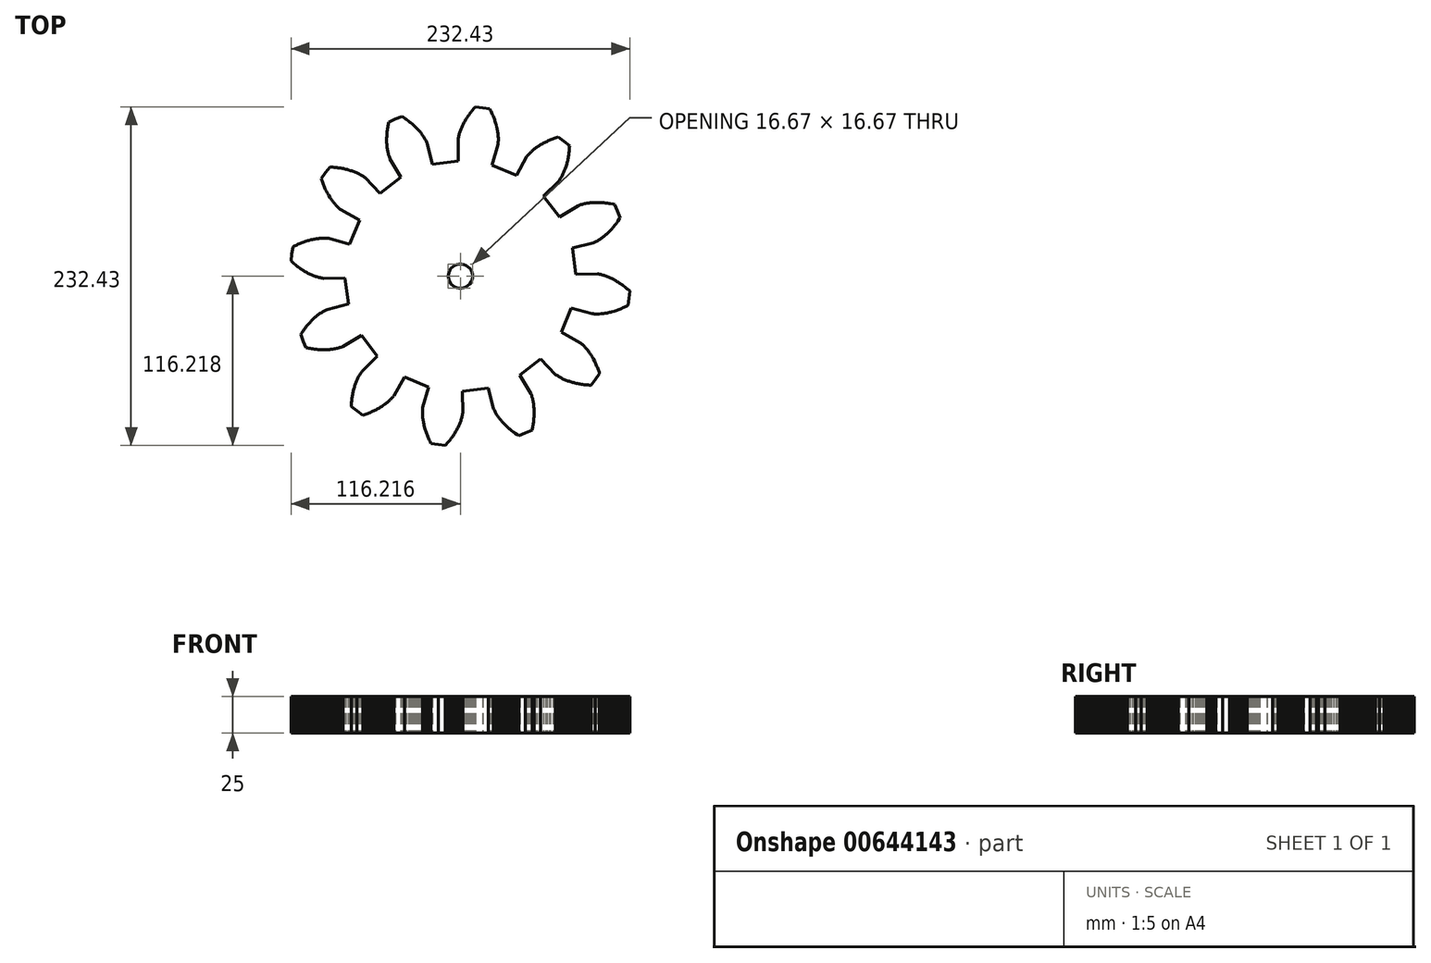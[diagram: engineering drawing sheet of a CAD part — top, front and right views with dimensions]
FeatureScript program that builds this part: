
annotation { "Feature Type Name" : "Feature", "Feature Type Description" : "" }
export const myFeature = defineFeature(function(context is Context, id is Id, definition is map)
    precondition{}
    {
        {
            var Q0;
            Q0=qCreatedBy(makeId("Top.planeOp"),FACE);
            var sketch = newSketch(context, id + "F0", { "sketchPlane" : qUnion([Q0])});
            skLineSegment(sketch, "E0", {"start": v(-581.55, 906.2) * mm, "end": v(-580.8, 906) * mm});
            skLineSegment(sketch, "E1", {"start": v(-580.8, 906) * mm, "end": v(-580.03, 905.86) * mm});
            skLineSegment(sketch, "E2", {"start": v(-580.03, 905.86) * mm, "end": v(-579.27, 905.7) * mm});
            skLineSegment(sketch, "E3", {"start": v(-579.27, 905.7) * mm, "end": v(-578.52, 905.52) * mm});
            skLineSegment(sketch, "E4", {"start": v(-578.52, 905.52) * mm, "end": v(-577.76, 905.33) * mm});
            skLineSegment(sketch, "E5", {"start": v(-577.76, 905.33) * mm, "end": v(-577, 905.1) * mm});
            skLineSegment(sketch, "E6", {"start": v(-577, 905.1) * mm, "end": v(-576.24, 904.85) * mm});
            skLineSegment(sketch, "E7", {"start": v(-576.24, 904.85) * mm, "end": v(-575.48, 904.59) * mm});
            skLineSegment(sketch, "E8", {"start": v(-575.48, 904.59) * mm, "end": v(-574.72, 904.3) * mm});
            skLineSegment(sketch, "E9", {"start": v(-574.72, 904.3) * mm, "end": v(-573.97, 904) * mm});
            skLineSegment(sketch, "E10", {"start": v(-573.97, 904) * mm, "end": v(-573.2, 903.67) * mm});
            skLineSegment(sketch, "E11", {"start": v(-573.2, 903.67) * mm, "end": v(-572.47, 903.34) * mm});
            skLineSegment(sketch, "E12", {"start": v(-572.47, 903.34) * mm, "end": v(-571.7, 902.97) * mm});
            skLineSegment(sketch, "E13", {"start": v(-571.7, 902.97) * mm, "end": v(-570.97, 902.6) * mm});
            skLineSegment(sketch, "E14", {"start": v(-570.97, 902.6) * mm, "end": v(-570.2, 902.2) * mm});
            skLineSegment(sketch, "E15", {"start": v(-570.2, 902.2) * mm, "end": v(-569.47, 901.78) * mm});
            skLineSegment(sketch, "E16", {"start": v(-569.47, 901.78) * mm, "end": v(-568.73, 901.34) * mm});
            skLineSegment(sketch, "E17", {"start": v(-568.73, 901.34) * mm, "end": v(-567.97, 900.9) * mm});
            skLineSegment(sketch, "E18", {"start": v(-567.97, 900.9) * mm, "end": v(-567.23, 900.44) * mm});
            skLineSegment(sketch, "E19", {"start": v(-567.23, 900.44) * mm, "end": v(-566.5, 899.95) * mm});
            skLineSegment(sketch, "E20", {"start": v(-566.5, 899.95) * mm, "end": v(-565.76, 899.46) * mm});
            skLineSegment(sketch, "E21", {"start": v(-565.76, 899.46) * mm, "end": v(-565.02, 898.95) * mm});
            skLineSegment(sketch, "E22", {"start": v(-565.02, 898.95) * mm, "end": v(-564.3, 898.42) * mm});
            skLineSegment(sketch, "E23", {"start": v(-564.3, 898.42) * mm, "end": v(-563.58, 897.87) * mm});
            skLineSegment(sketch, "E24", {"start": v(-563.58, 897.87) * mm, "end": v(-562.85, 897.3) * mm});
            skLineSegment(sketch, "E25", {"start": v(-562.85, 897.3) * mm, "end": v(-562.13, 896.72) * mm});
            skLineSegment(sketch, "E26", {"start": v(-562.13, 896.72) * mm, "end": v(-561.42, 896.14) * mm});
            skLineSegment(sketch, "E27", {"start": v(-561.42, 896.14) * mm, "end": v(-560.7, 895.52) * mm});
            skLineSegment(sketch, "E28", {"start": v(-560.7, 895.52) * mm, "end": v(-560, 894.9) * mm});
            skLineSegment(sketch, "E29", {"start": v(-560, 894.9) * mm, "end": v(-559.29, 894.25) * mm});
            skLineSegment(sketch, "E30", {"start": v(-559.29, 894.25) * mm, "end": v(-559.84, 889.37) * mm});
            skLineSegment(sketch, "E31", {"start": v(-559.84, 889.37) * mm, "end": v(-560.58, 884.5) * mm});
            skLineSegment(sketch, "E32", {"start": v(-560.58, 884.5) * mm, "end": v(-561.42, 884.06) * mm});
            skLineSegment(sketch, "E33", {"start": v(-561.42, 884.06) * mm, "end": v(-562.27, 883.65) * mm});
            skLineSegment(sketch, "E34", {"start": v(-562.27, 883.65) * mm, "end": v(-563.12, 883.25) * mm});
            skLineSegment(sketch, "E35", {"start": v(-563.12, 883.25) * mm, "end": v(-563.96, 882.86) * mm});
            skLineSegment(sketch, "E36", {"start": v(-563.96, 882.86) * mm, "end": v(-564.81, 882.47) * mm});
            skLineSegment(sketch, "E37", {"start": v(-564.81, 882.47) * mm, "end": v(-565.64, 882.12) * mm});
            skLineSegment(sketch, "E38", {"start": v(-565.64, 882.12) * mm, "end": v(-566.49, 881.78) * mm});
            skLineSegment(sketch, "E39", {"start": v(-566.49, 881.78) * mm, "end": v(-567.33, 881.47) * mm});
            skLineSegment(sketch, "E40", {"start": v(-567.33, 881.47) * mm, "end": v(-568.18, 881.15) * mm});
            skLineSegment(sketch, "E41", {"start": v(-568.18, 881.15) * mm, "end": v(-569, 880.87) * mm});
            skLineSegment(sketch, "E42", {"start": v(-569, 880.87) * mm, "end": v(-569.86, 880.58) * mm});
            skLineSegment(sketch, "E43", {"start": v(-569.86, 880.58) * mm, "end": v(-570.68, 880.34) * mm});
            skLineSegment(sketch, "E44", {"start": v(-570.68, 880.34) * mm, "end": v(-571.51, 880.09) * mm});
            skLineSegment(sketch, "E45", {"start": v(-571.51, 880.09) * mm, "end": v(-572.34, 879.88) * mm});
            skLineSegment(sketch, "E46", {"start": v(-572.34, 879.88) * mm, "end": v(-573.17, 879.67) * mm});
            skLineSegment(sketch, "E47", {"start": v(-573.17, 879.67) * mm, "end": v(-574, 879.47) * mm});
            skLineSegment(sketch, "E48", {"start": v(-574, 879.47) * mm, "end": v(-574.83, 879.3) * mm});
            skLineSegment(sketch, "E49", {"start": v(-574.83, 879.3) * mm, "end": v(-575.64, 879.15) * mm});
            skLineSegment(sketch, "E50", {"start": v(-575.64, 879.15) * mm, "end": v(-576.45, 879.01) * mm});
            skLineSegment(sketch, "E51", {"start": v(-576.45, 879.01) * mm, "end": v(-577.26, 878.89) * mm});
            skLineSegment(sketch, "E52", {"start": v(-577.26, 878.89) * mm, "end": v(-578.08, 878.8) * mm});
            skLineSegment(sketch, "E53", {"start": v(-578.08, 878.8) * mm, "end": v(-578.89, 878.71) * mm});
            skLineSegment(sketch, "E54", {"start": v(-578.89, 878.71) * mm, "end": v(-579.68, 878.66) * mm});
            skLineSegment(sketch, "E55", {"start": v(-579.68, 878.66) * mm, "end": v(-580.47, 878.6) * mm});
            skLineSegment(sketch, "E56", {"start": v(-580.47, 878.6) * mm, "end": v(-581.27, 878.6) * mm});
            skLineSegment(sketch, "E57", {"start": v(-581.27, 878.6) * mm, "end": v(-582.06, 878.6) * mm});
            skLineSegment(sketch, "E58", {"start": v(-582.06, 878.6) * mm, "end": v(-582.84, 878.62) * mm});
            skLineSegment(sketch, "E59", {"start": v(-582.84, 878.62) * mm, "end": v(-583.61, 878.66) * mm});
            skLineSegment(sketch, "E60", {"start": v(-583.61, 878.66) * mm, "end": v(-584.37, 878.73) * mm});
            skLineSegment(sketch, "E61", {"start": v(-584.37, 878.73) * mm, "end": v(-585.17, 878.73) * mm});
            skLineSegment(sketch, "E62", {"start": v(-585.17, 878.73) * mm, "end": v(-599.38, 882.8) * mm});
            skLineSegment(sketch, "E63", {"start": v(-599.38, 882.8) * mm, "end": v(-606.28, 866.17) * mm});
            skLineSegment(sketch, "E64", {"start": v(-606.28, 866.17) * mm, "end": v(-593.33, 859) * mm});
            skLineSegment(sketch, "E65", {"start": v(-593.33, 859) * mm, "end": v(-592.77, 858.45) * mm});
            skLineSegment(sketch, "E66", {"start": v(-592.77, 858.45) * mm, "end": v(-592.19, 857.95) * mm});
            skLineSegment(sketch, "E67", {"start": v(-592.19, 857.95) * mm, "end": v(-591.6, 857.44) * mm});
            skLineSegment(sketch, "E68", {"start": v(-591.6, 857.44) * mm, "end": v(-591.04, 856.91) * mm});
            skLineSegment(sketch, "E69", {"start": v(-591.04, 856.91) * mm, "end": v(-590.48, 856.35) * mm});
            skLineSegment(sketch, "E70", {"start": v(-590.48, 856.35) * mm, "end": v(-589.95, 855.78) * mm});
            skLineSegment(sketch, "E71", {"start": v(-589.95, 855.78) * mm, "end": v(-589.4, 855.18) * mm});
            skLineSegment(sketch, "E72", {"start": v(-589.4, 855.18) * mm, "end": v(-588.89, 854.58) * mm});
            skLineSegment(sketch, "E73", {"start": v(-588.89, 854.58) * mm, "end": v(-588.38, 853.95) * mm});
            skLineSegment(sketch, "E74", {"start": v(-588.38, 853.95) * mm, "end": v(-587.86, 853.31) * mm});
            skLineSegment(sketch, "E75", {"start": v(-587.86, 853.31) * mm, "end": v(-587.37, 852.64) * mm});
            skLineSegment(sketch, "E76", {"start": v(-587.37, 852.64) * mm, "end": v(-586.9, 851.97) * mm});
            skLineSegment(sketch, "E77", {"start": v(-586.9, 851.97) * mm, "end": v(-586.44, 851.28) * mm});
            skLineSegment(sketch, "E78", {"start": v(-586.44, 851.28) * mm, "end": v(-585.96, 850.58) * mm});
            skLineSegment(sketch, "E79", {"start": v(-585.96, 850.58) * mm, "end": v(-585.52, 849.87) * mm});
            skLineSegment(sketch, "E80", {"start": v(-585.52, 849.87) * mm, "end": v(-585.08, 849.13) * mm});
            skLineSegment(sketch, "E81", {"start": v(-585.08, 849.13) * mm, "end": v(-584.65, 848.4) * mm});
            skLineSegment(sketch, "E82", {"start": v(-584.65, 848.4) * mm, "end": v(-584.23, 847.63) * mm});
            skLineSegment(sketch, "E83", {"start": v(-584.23, 847.63) * mm, "end": v(-583.83, 846.86) * mm});
            skLineSegment(sketch, "E84", {"start": v(-583.83, 846.86) * mm, "end": v(-583.42, 846.08) * mm});
            skLineSegment(sketch, "E85", {"start": v(-583.42, 846.08) * mm, "end": v(-583.03, 845.27) * mm});
            skLineSegment(sketch, "E86", {"start": v(-583.03, 845.27) * mm, "end": v(-582.66, 844.46) * mm});
            skLineSegment(sketch, "E87", {"start": v(-582.66, 844.46) * mm, "end": v(-582.3, 843.65) * mm});
            skLineSegment(sketch, "E88", {"start": v(-582.3, 843.65) * mm, "end": v(-581.94, 842.8) * mm});
            skLineSegment(sketch, "E89", {"start": v(-581.94, 842.8) * mm, "end": v(-581.59, 841.95) * mm});
            skLineSegment(sketch, "E90", {"start": v(-581.59, 841.95) * mm, "end": v(-581.25, 841.09) * mm});
            skLineSegment(sketch, "E91", {"start": v(-581.25, 841.09) * mm, "end": v(-580.93, 840.23) * mm});
            skLineSegment(sketch, "E92", {"start": v(-580.93, 840.23) * mm, "end": v(-580.62, 839.34) * mm});
            skLineSegment(sketch, "E93", {"start": v(-580.62, 839.34) * mm, "end": v(-580.32, 838.44) * mm});
            skLineSegment(sketch, "E94", {"start": v(-580.32, 838.44) * mm, "end": v(-580.03, 837.54) * mm});
            skLineSegment(sketch, "E95", {"start": v(-580.03, 837.54) * mm, "end": v(-582.94, 833.58) * mm});
            skLineSegment(sketch, "E96", {"start": v(-582.94, 833.58) * mm, "end": v(-586.01, 829.73) * mm});
            skLineSegment(sketch, "E97", {"start": v(-586.01, 829.73) * mm, "end": v(-586.97, 829.78) * mm});
            skLineSegment(sketch, "E98", {"start": v(-586.97, 829.78) * mm, "end": v(-587.92, 829.84) * mm});
            skLineSegment(sketch, "E99", {"start": v(-587.92, 829.84) * mm, "end": v(-588.85, 829.9) * mm});
            skLineSegment(sketch, "E100", {"start": v(-588.85, 829.9) * mm, "end": v(-589.77, 830) * mm});
            skLineSegment(sketch, "E101", {"start": v(-589.77, 830) * mm, "end": v(-590.69, 830.1) * mm});
            skLineSegment(sketch, "E102", {"start": v(-590.69, 830.1) * mm, "end": v(-591.6, 830.2) * mm});
            skLineSegment(sketch, "E103", {"start": v(-591.6, 830.2) * mm, "end": v(-592.5, 830.33) * mm});
            skLineSegment(sketch, "E104", {"start": v(-592.5, 830.33) * mm, "end": v(-593.39, 830.47) * mm});
            skLineSegment(sketch, "E105", {"start": v(-593.39, 830.47) * mm, "end": v(-594.27, 830.63) * mm});
            skLineSegment(sketch, "E106", {"start": v(-594.27, 830.63) * mm, "end": v(-595.15, 830.79) * mm});
            skLineSegment(sketch, "E107", {"start": v(-595.15, 830.79) * mm, "end": v(-596.01, 830.98) * mm});
            skLineSegment(sketch, "E108", {"start": v(-596.01, 830.98) * mm, "end": v(-596.86, 831.18) * mm});
            skLineSegment(sketch, "E109", {"start": v(-596.86, 831.18) * mm, "end": v(-597.7, 831.39) * mm});
            skLineSegment(sketch, "E110", {"start": v(-597.7, 831.39) * mm, "end": v(-598.54, 831.6) * mm});
            skLineSegment(sketch, "E111", {"start": v(-598.54, 831.6) * mm, "end": v(-599.35, 831.85) * mm});
            skLineSegment(sketch, "E112", {"start": v(-599.35, 831.85) * mm, "end": v(-600.16, 832.1) * mm});
            skLineSegment(sketch, "E113", {"start": v(-600.16, 832.1) * mm, "end": v(-600.95, 832.36) * mm});
            skLineSegment(sketch, "E114", {"start": v(-600.95, 832.36) * mm, "end": v(-601.75, 832.62) * mm});
            skLineSegment(sketch, "E115", {"start": v(-601.75, 832.62) * mm, "end": v(-602.52, 832.92) * mm});
            skLineSegment(sketch, "E116", {"start": v(-602.52, 832.92) * mm, "end": v(-603.28, 833.22) * mm});
            skLineSegment(sketch, "E117", {"start": v(-603.28, 833.22) * mm, "end": v(-604.04, 833.54) * mm});
            skLineSegment(sketch, "E118", {"start": v(-604.04, 833.54) * mm, "end": v(-604.76, 833.88) * mm});
            skLineSegment(sketch, "E119", {"start": v(-604.76, 833.88) * mm, "end": v(-605.49, 834.23) * mm});
            skLineSegment(sketch, "E120", {"start": v(-605.49, 834.23) * mm, "end": v(-606.2, 834.58) * mm});
            skLineSegment(sketch, "E121", {"start": v(-606.2, 834.58) * mm, "end": v(-606.9, 834.95) * mm});
            skLineSegment(sketch, "E122", {"start": v(-606.9, 834.95) * mm, "end": v(-607.57, 835.36) * mm});
            skLineSegment(sketch, "E123", {"start": v(-607.57, 835.36) * mm, "end": v(-608.24, 835.76) * mm});
            skLineSegment(sketch, "E124", {"start": v(-608.24, 835.76) * mm, "end": v(-608.9, 836.19) * mm});
            skLineSegment(sketch, "E125", {"start": v(-608.9, 836.19) * mm, "end": v(-609.53, 836.63) * mm});
            skLineSegment(sketch, "E126", {"start": v(-609.53, 836.63) * mm, "end": v(-610.2, 837.03) * mm});
            skLineSegment(sketch, "E127", {"start": v(-610.2, 837.03) * mm, "end": v(-620.48, 847.67) * mm});
            skLineSegment(sketch, "E128", {"start": v(-620.48, 847.67) * mm, "end": v(-634.77, 836.72) * mm});
            skLineSegment(sketch, "E129", {"start": v(-634.77, 836.72) * mm, "end": v(-627.15, 824.02) * mm});
            skLineSegment(sketch, "E130", {"start": v(-627.15, 824.02) * mm, "end": v(-626.93, 823.27) * mm});
            skLineSegment(sketch, "E131", {"start": v(-626.93, 823.27) * mm, "end": v(-626.67, 822.55) * mm});
            skLineSegment(sketch, "E132", {"start": v(-626.67, 822.55) * mm, "end": v(-626.42, 821.8) * mm});
            skLineSegment(sketch, "E133", {"start": v(-626.42, 821.8) * mm, "end": v(-626.2, 821.07) * mm});
            skLineSegment(sketch, "E134", {"start": v(-626.2, 821.07) * mm, "end": v(-626, 820.31) * mm});
            skLineSegment(sketch, "E135", {"start": v(-626, 820.31) * mm, "end": v(-625.8, 819.54) * mm});
            skLineSegment(sketch, "E136", {"start": v(-625.8, 819.54) * mm, "end": v(-625.65, 818.76) * mm});
            skLineSegment(sketch, "E137", {"start": v(-625.65, 818.76) * mm, "end": v(-625.5, 817.97) * mm});
            skLineSegment(sketch, "E138", {"start": v(-625.5, 817.97) * mm, "end": v(-625.37, 817.17) * mm});
            skLineSegment(sketch, "E139", {"start": v(-625.37, 817.17) * mm, "end": v(-625.26, 816.36) * mm});
            skLineSegment(sketch, "E140", {"start": v(-625.26, 816.36) * mm, "end": v(-625.15, 815.55) * mm});
            skLineSegment(sketch, "E141", {"start": v(-625.15, 815.55) * mm, "end": v(-625.08, 814.72) * mm});
            skLineSegment(sketch, "E142", {"start": v(-625.08, 814.72) * mm, "end": v(-625.01, 813.9) * mm});
            skLineSegment(sketch, "E143", {"start": v(-625.01, 813.9) * mm, "end": v(-624.96, 813.06) * mm});
            skLineSegment(sketch, "E144", {"start": v(-624.96, 813.06) * mm, "end": v(-624.94, 812.21) * mm});
            skLineSegment(sketch, "E145", {"start": v(-624.94, 812.21) * mm, "end": v(-624.92, 811.35) * mm});
            skLineSegment(sketch, "E146", {"start": v(-624.92, 811.35) * mm, "end": v(-624.92, 810.49) * mm});
            skLineSegment(sketch, "E147", {"start": v(-624.92, 810.49) * mm, "end": v(-624.94, 809.62) * mm});
            skLineSegment(sketch, "E148", {"start": v(-624.94, 809.62) * mm, "end": v(-624.98, 808.76) * mm});
            skLineSegment(sketch, "E149", {"start": v(-624.98, 808.76) * mm, "end": v(-625.01, 807.88) * mm});
            skLineSegment(sketch, "E150", {"start": v(-625.01, 807.88) * mm, "end": v(-625.08, 807) * mm});
            skLineSegment(sketch, "E151", {"start": v(-625.08, 807) * mm, "end": v(-625.15, 806.1) * mm});
            skLineSegment(sketch, "E152", {"start": v(-625.15, 806.1) * mm, "end": v(-625.26, 805.2) * mm});
            skLineSegment(sketch, "E153", {"start": v(-625.26, 805.2) * mm, "end": v(-625.37, 804.3) * mm});
            skLineSegment(sketch, "E154", {"start": v(-625.37, 804.3) * mm, "end": v(-625.49, 803.4) * mm});
            skLineSegment(sketch, "E155", {"start": v(-625.49, 803.4) * mm, "end": v(-625.63, 802.48) * mm});
            skLineSegment(sketch, "E156", {"start": v(-625.63, 802.48) * mm, "end": v(-625.79, 801.56) * mm});
            skLineSegment(sketch, "E157", {"start": v(-625.79, 801.56) * mm, "end": v(-625.96, 800.64) * mm});
            skLineSegment(sketch, "E158", {"start": v(-625.96, 800.64) * mm, "end": v(-626.14, 799.7) * mm});
            skLineSegment(sketch, "E159", {"start": v(-626.14, 799.7) * mm, "end": v(-626.35, 798.8) * mm});
            skLineSegment(sketch, "E160", {"start": v(-626.35, 798.8) * mm, "end": v(-630.85, 796.8) * mm});
            skLineSegment(sketch, "E161", {"start": v(-630.85, 796.8) * mm, "end": v(-635.44, 795.02) * mm});
            skLineSegment(sketch, "E162", {"start": v(-635.44, 795.02) * mm, "end": v(-636.25, 795.53) * mm});
            skLineSegment(sketch, "E163", {"start": v(-636.25, 795.53) * mm, "end": v(-637.02, 796.06) * mm});
            skLineSegment(sketch, "E164", {"start": v(-637.02, 796.06) * mm, "end": v(-637.8, 796.59) * mm});
            skLineSegment(sketch, "E165", {"start": v(-637.8, 796.59) * mm, "end": v(-638.56, 797.12) * mm});
            skLineSegment(sketch, "E166", {"start": v(-638.56, 797.12) * mm, "end": v(-639.3, 797.66) * mm});
            skLineSegment(sketch, "E167", {"start": v(-639.3, 797.66) * mm, "end": v(-640.04, 798.23) * mm});
            skLineSegment(sketch, "E168", {"start": v(-640.04, 798.23) * mm, "end": v(-640.75, 798.77) * mm});
            skLineSegment(sketch, "E169", {"start": v(-640.75, 798.77) * mm, "end": v(-641.45, 799.36) * mm});
            skLineSegment(sketch, "E170", {"start": v(-641.45, 799.36) * mm, "end": v(-642.14, 799.92) * mm});
            skLineSegment(sketch, "E171", {"start": v(-642.14, 799.92) * mm, "end": v(-642.8, 800.5) * mm});
            skLineSegment(sketch, "E172", {"start": v(-642.8, 800.5) * mm, "end": v(-643.46, 801.08) * mm});
            skLineSegment(sketch, "E173", {"start": v(-643.46, 801.08) * mm, "end": v(-644.12, 801.68) * mm});
            skLineSegment(sketch, "E174", {"start": v(-644.12, 801.68) * mm, "end": v(-644.73, 802.28) * mm});
            skLineSegment(sketch, "E175", {"start": v(-644.73, 802.28) * mm, "end": v(-645.33, 802.9) * mm});
            skLineSegment(sketch, "E176", {"start": v(-645.33, 802.9) * mm, "end": v(-645.93, 803.52) * mm});
            skLineSegment(sketch, "E177", {"start": v(-645.93, 803.52) * mm, "end": v(-646.51, 804.14) * mm});
            skLineSegment(sketch, "E178", {"start": v(-646.51, 804.14) * mm, "end": v(-647.06, 804.75) * mm});
            skLineSegment(sketch, "E179", {"start": v(-647.06, 804.75) * mm, "end": v(-647.6, 805.39) * mm});
            skLineSegment(sketch, "E180", {"start": v(-647.6, 805.39) * mm, "end": v(-648.14, 806.02) * mm});
            skLineSegment(sketch, "E181", {"start": v(-648.14, 806.02) * mm, "end": v(-648.65, 806.68) * mm});
            skLineSegment(sketch, "E182", {"start": v(-648.65, 806.68) * mm, "end": v(-649.14, 807.33) * mm});
            skLineSegment(sketch, "E183", {"start": v(-649.14, 807.33) * mm, "end": v(-649.6, 807.98) * mm});
            skLineSegment(sketch, "E184", {"start": v(-649.6, 807.98) * mm, "end": v(-650.06, 808.65) * mm});
            skLineSegment(sketch, "E185", {"start": v(-650.06, 808.65) * mm, "end": v(-650.5, 809.3) * mm});
            skLineSegment(sketch, "E186", {"start": v(-650.5, 809.3) * mm, "end": v(-650.9, 810) * mm});
            skLineSegment(sketch, "E187", {"start": v(-650.9, 810) * mm, "end": v(-651.3, 810.66) * mm});
            skLineSegment(sketch, "E188", {"start": v(-651.3, 810.66) * mm, "end": v(-651.66, 811.35) * mm});
            skLineSegment(sketch, "E189", {"start": v(-651.66, 811.35) * mm, "end": v(-652.02, 812.04) * mm});
            skLineSegment(sketch, "E190", {"start": v(-652.02, 812.04) * mm, "end": v(-652.33, 812.74) * mm});
            skLineSegment(sketch, "E191", {"start": v(-652.33, 812.74) * mm, "end": v(-652.72, 813.43) * mm});
            skLineSegment(sketch, "E192", {"start": v(-652.72, 813.43) * mm, "end": v(-656.3, 827.8) * mm});
            skLineSegment(sketch, "E193", {"start": v(-656.3, 827.8) * mm, "end": v(-674.15, 825.44) * mm});
            skLineSegment(sketch, "E194", {"start": v(-674.15, 825.44) * mm, "end": v(-673.9, 810.64) * mm});
            skLineSegment(sketch, "E195", {"start": v(-673.9, 810.64) * mm, "end": v(-674.1, 809.87) * mm});
            skLineSegment(sketch, "E196", {"start": v(-674.1, 809.87) * mm, "end": v(-674.24, 809.11) * mm});
            skLineSegment(sketch, "E197", {"start": v(-674.24, 809.11) * mm, "end": v(-674.4, 808.35) * mm});
            skLineSegment(sketch, "E198", {"start": v(-674.4, 808.35) * mm, "end": v(-674.58, 807.6) * mm});
            skLineSegment(sketch, "E199", {"start": v(-674.58, 807.6) * mm, "end": v(-674.77, 806.84) * mm});
            skLineSegment(sketch, "E200", {"start": v(-674.77, 806.84) * mm, "end": v(-675, 806.08) * mm});
            skLineSegment(sketch, "E201", {"start": v(-675, 806.08) * mm, "end": v(-675.25, 805.34) * mm});
            skLineSegment(sketch, "E202", {"start": v(-675.25, 805.34) * mm, "end": v(-675.51, 804.58) * mm});
            skLineSegment(sketch, "E203", {"start": v(-675.51, 804.58) * mm, "end": v(-675.8, 803.82) * mm});
            skLineSegment(sketch, "E204", {"start": v(-675.8, 803.82) * mm, "end": v(-676.1, 803.06) * mm});
            skLineSegment(sketch, "E205", {"start": v(-676.1, 803.06) * mm, "end": v(-676.43, 802.3) * mm});
            skLineSegment(sketch, "E206", {"start": v(-676.43, 802.3) * mm, "end": v(-676.76, 801.54) * mm});
            skLineSegment(sketch, "E207", {"start": v(-676.76, 801.54) * mm, "end": v(-677.14, 800.8) * mm});
            skLineSegment(sketch, "E208", {"start": v(-677.14, 800.8) * mm, "end": v(-677.5, 800.04) * mm});
            skLineSegment(sketch, "E209", {"start": v(-677.5, 800.04) * mm, "end": v(-677.91, 799.3) * mm});
            skLineSegment(sketch, "E210", {"start": v(-677.91, 799.3) * mm, "end": v(-678.32, 798.56) * mm});
            skLineSegment(sketch, "E211", {"start": v(-678.32, 798.56) * mm, "end": v(-678.74, 797.8) * mm});
            skLineSegment(sketch, "E212", {"start": v(-678.74, 797.8) * mm, "end": v(-679.2, 797.06) * mm});
            skLineSegment(sketch, "E213", {"start": v(-679.2, 797.06) * mm, "end": v(-679.66, 796.32) * mm});
            skLineSegment(sketch, "E214", {"start": v(-679.66, 796.32) * mm, "end": v(-680.13, 795.58) * mm});
            skLineSegment(sketch, "E215", {"start": v(-680.13, 795.58) * mm, "end": v(-680.65, 794.86) * mm});
            skLineSegment(sketch, "E216", {"start": v(-680.65, 794.86) * mm, "end": v(-681.16, 794.12) * mm});
            skLineSegment(sketch, "E217", {"start": v(-681.16, 794.12) * mm, "end": v(-681.69, 793.4) * mm});
            skLineSegment(sketch, "E218", {"start": v(-681.69, 793.4) * mm, "end": v(-682.23, 792.67) * mm});
            skLineSegment(sketch, "E219", {"start": v(-682.23, 792.67) * mm, "end": v(-682.8, 791.95) * mm});
            skLineSegment(sketch, "E220", {"start": v(-682.8, 791.95) * mm, "end": v(-683.36, 791.22) * mm});
            skLineSegment(sketch, "E221", {"start": v(-683.36, 791.22) * mm, "end": v(-683.96, 790.5) * mm});
            skLineSegment(sketch, "E222", {"start": v(-683.96, 790.5) * mm, "end": v(-684.58, 789.8) * mm});
            skLineSegment(sketch, "E223", {"start": v(-684.58, 789.8) * mm, "end": v(-685.2, 789.1) * mm});
            skLineSegment(sketch, "E224", {"start": v(-685.2, 789.1) * mm, "end": v(-685.85, 788.38) * mm});
            skLineSegment(sketch, "E225", {"start": v(-685.85, 788.38) * mm, "end": v(-690.73, 788.93) * mm});
            skLineSegment(sketch, "E226", {"start": v(-690.73, 788.93) * mm, "end": v(-695.6, 789.67) * mm});
            skLineSegment(sketch, "E227", {"start": v(-695.6, 789.67) * mm, "end": v(-696.03, 790.52) * mm});
            skLineSegment(sketch, "E228", {"start": v(-696.03, 790.52) * mm, "end": v(-696.45, 791.37) * mm});
            skLineSegment(sketch, "E229", {"start": v(-696.45, 791.37) * mm, "end": v(-696.86, 792.21) * mm});
            skLineSegment(sketch, "E230", {"start": v(-696.86, 792.21) * mm, "end": v(-697.24, 793.06) * mm});
            skLineSegment(sketch, "E231", {"start": v(-697.24, 793.06) * mm, "end": v(-697.61, 793.89) * mm});
            skLineSegment(sketch, "E232", {"start": v(-697.61, 793.89) * mm, "end": v(-697.98, 794.73) * mm});
            skLineSegment(sketch, "E233", {"start": v(-697.98, 794.73) * mm, "end": v(-698.32, 795.58) * mm});
            skLineSegment(sketch, "E234", {"start": v(-698.32, 795.58) * mm, "end": v(-698.64, 796.43) * mm});
            skLineSegment(sketch, "E235", {"start": v(-698.64, 796.43) * mm, "end": v(-698.95, 797.26) * mm});
            skLineSegment(sketch, "E236", {"start": v(-698.95, 797.26) * mm, "end": v(-699.24, 798.1) * mm});
            skLineSegment(sketch, "E237", {"start": v(-699.24, 798.1) * mm, "end": v(-699.52, 798.93) * mm});
            skLineSegment(sketch, "E238", {"start": v(-699.52, 798.93) * mm, "end": v(-699.77, 799.78) * mm});
            skLineSegment(sketch, "E239", {"start": v(-699.77, 799.78) * mm, "end": v(-700.01, 800.6) * mm});
            skLineSegment(sketch, "E240", {"start": v(-700.01, 800.6) * mm, "end": v(-700.22, 801.44) * mm});
            skLineSegment(sketch, "E241", {"start": v(-700.22, 801.44) * mm, "end": v(-700.44, 802.27) * mm});
            skLineSegment(sketch, "E242", {"start": v(-700.44, 802.27) * mm, "end": v(-700.63, 803.1) * mm});
            skLineSegment(sketch, "E243", {"start": v(-700.63, 803.1) * mm, "end": v(-700.79, 803.92) * mm});
            skLineSegment(sketch, "E244", {"start": v(-700.79, 803.92) * mm, "end": v(-700.95, 804.74) * mm});
            skLineSegment(sketch, "E245", {"start": v(-700.95, 804.74) * mm, "end": v(-701.09, 805.55) * mm});
            skLineSegment(sketch, "E246", {"start": v(-701.09, 805.55) * mm, "end": v(-701.21, 806.36) * mm});
            skLineSegment(sketch, "E247", {"start": v(-701.21, 806.36) * mm, "end": v(-701.3, 807.17) * mm});
            skLineSegment(sketch, "E248", {"start": v(-701.3, 807.17) * mm, "end": v(-701.39, 807.98) * mm});
            skLineSegment(sketch, "E249", {"start": v(-701.39, 807.98) * mm, "end": v(-701.44, 808.78) * mm});
            skLineSegment(sketch, "E250", {"start": v(-701.44, 808.78) * mm, "end": v(-701.5, 809.57) * mm});
            skLineSegment(sketch, "E251", {"start": v(-701.5, 809.57) * mm, "end": v(-701.51, 810.36) * mm});
            skLineSegment(sketch, "E252", {"start": v(-701.51, 810.36) * mm, "end": v(-701.51, 811.14) * mm});
            skLineSegment(sketch, "E253", {"start": v(-701.51, 811.14) * mm, "end": v(-701.48, 811.93) * mm});
            skLineSegment(sketch, "E254", {"start": v(-701.48, 811.93) * mm, "end": v(-701.44, 812.7) * mm});
            skLineSegment(sketch, "E255", {"start": v(-701.44, 812.7) * mm, "end": v(-701.37, 813.47) * mm});
            skLineSegment(sketch, "E256", {"start": v(-701.37, 813.47) * mm, "end": v(-701.35, 814.24) * mm});
            skLineSegment(sketch, "E257", {"start": v(-701.35, 814.24) * mm, "end": v(-697.28, 828.48) * mm});
            skLineSegment(sketch, "E258", {"start": v(-697.28, 828.48) * mm, "end": v(-713.93, 835.37) * mm});
            skLineSegment(sketch, "E259", {"start": v(-713.93, 835.37) * mm, "end": v(-721.1, 822.43) * mm});
            skLineSegment(sketch, "E260", {"start": v(-721.1, 822.43) * mm, "end": v(-721.66, 821.86) * mm});
            skLineSegment(sketch, "E261", {"start": v(-721.66, 821.86) * mm, "end": v(-722.15, 821.28) * mm});
            skLineSegment(sketch, "E262", {"start": v(-722.15, 821.28) * mm, "end": v(-722.66, 820.7) * mm});
            skLineSegment(sketch, "E263", {"start": v(-722.66, 820.7) * mm, "end": v(-723.2, 820.13) * mm});
            skLineSegment(sketch, "E264", {"start": v(-723.2, 820.13) * mm, "end": v(-723.75, 819.57) * mm});
            skLineSegment(sketch, "E265", {"start": v(-723.75, 819.57) * mm, "end": v(-724.32, 819.02) * mm});
            skLineSegment(sketch, "E266", {"start": v(-724.32, 819.02) * mm, "end": v(-724.92, 818.5) * mm});
            skLineSegment(sketch, "E267", {"start": v(-724.92, 818.5) * mm, "end": v(-725.52, 817.98) * mm});
            skLineSegment(sketch, "E268", {"start": v(-725.52, 817.98) * mm, "end": v(-726.15, 817.47) * mm});
            skLineSegment(sketch, "E269", {"start": v(-726.15, 817.47) * mm, "end": v(-726.79, 816.96) * mm});
            skLineSegment(sketch, "E270", {"start": v(-726.79, 816.96) * mm, "end": v(-727.44, 816.47) * mm});
            skLineSegment(sketch, "E271", {"start": v(-727.44, 816.47) * mm, "end": v(-728.13, 815.99) * mm});
            skLineSegment(sketch, "E272", {"start": v(-728.13, 815.99) * mm, "end": v(-728.82, 815.51) * mm});
            skLineSegment(sketch, "E273", {"start": v(-728.82, 815.51) * mm, "end": v(-729.5, 815.05) * mm});
            skLineSegment(sketch, "E274", {"start": v(-729.5, 815.05) * mm, "end": v(-730.23, 814.61) * mm});
            skLineSegment(sketch, "E275", {"start": v(-730.23, 814.61) * mm, "end": v(-730.97, 814.17) * mm});
            skLineSegment(sketch, "E276", {"start": v(-730.97, 814.17) * mm, "end": v(-731.7, 813.73) * mm});
            skLineSegment(sketch, "E277", {"start": v(-731.7, 813.73) * mm, "end": v(-732.47, 813.33) * mm});
            skLineSegment(sketch, "E278", {"start": v(-732.47, 813.33) * mm, "end": v(-733.24, 812.9) * mm});
            skLineSegment(sketch, "E279", {"start": v(-733.24, 812.9) * mm, "end": v(-734.02, 812.51) * mm});
            skLineSegment(sketch, "E280", {"start": v(-734.02, 812.51) * mm, "end": v(-734.81, 812.13) * mm});
            skLineSegment(sketch, "E281", {"start": v(-734.81, 812.13) * mm, "end": v(-735.63, 811.76) * mm});
            skLineSegment(sketch, "E282", {"start": v(-735.63, 811.76) * mm, "end": v(-736.45, 811.38) * mm});
            skLineSegment(sketch, "E283", {"start": v(-736.45, 811.38) * mm, "end": v(-737.3, 811.03) * mm});
            skLineSegment(sketch, "E284", {"start": v(-737.3, 811.03) * mm, "end": v(-738.15, 810.68) * mm});
            skLineSegment(sketch, "E285", {"start": v(-738.15, 810.68) * mm, "end": v(-739, 810.35) * mm});
            skLineSegment(sketch, "E286", {"start": v(-739, 810.35) * mm, "end": v(-739.88, 810.03) * mm});
            skLineSegment(sketch, "E287", {"start": v(-739.88, 810.03) * mm, "end": v(-740.76, 809.7) * mm});
            skLineSegment(sketch, "E288", {"start": v(-740.76, 809.7) * mm, "end": v(-741.66, 809.41) * mm});
            skLineSegment(sketch, "E289", {"start": v(-741.66, 809.41) * mm, "end": v(-742.56, 809.13) * mm});
            skLineSegment(sketch, "E290", {"start": v(-742.56, 809.13) * mm, "end": v(-746.53, 812.04) * mm});
            skLineSegment(sketch, "E291", {"start": v(-746.53, 812.04) * mm, "end": v(-750.37, 815.1) * mm});
            skLineSegment(sketch, "E292", {"start": v(-750.37, 815.1) * mm, "end": v(-750.32, 816.06) * mm});
            skLineSegment(sketch, "E293", {"start": v(-750.32, 816.06) * mm, "end": v(-750.27, 817.01) * mm});
            skLineSegment(sketch, "E294", {"start": v(-750.27, 817.01) * mm, "end": v(-750.2, 817.95) * mm});
            skLineSegment(sketch, "E295", {"start": v(-750.2, 817.95) * mm, "end": v(-750.1, 818.86) * mm});
            skLineSegment(sketch, "E296", {"start": v(-750.1, 818.86) * mm, "end": v(-750, 819.78) * mm});
            skLineSegment(sketch, "E297", {"start": v(-750, 819.78) * mm, "end": v(-749.9, 820.7) * mm});
            skLineSegment(sketch, "E298", {"start": v(-749.9, 820.7) * mm, "end": v(-749.77, 821.6) * mm});
            skLineSegment(sketch, "E299", {"start": v(-749.77, 821.6) * mm, "end": v(-749.63, 822.48) * mm});
            skLineSegment(sketch, "E300", {"start": v(-749.63, 822.48) * mm, "end": v(-749.47, 823.36) * mm});
            skLineSegment(sketch, "E301", {"start": v(-749.47, 823.36) * mm, "end": v(-749.3, 824.24) * mm});
            skLineSegment(sketch, "E302", {"start": v(-749.3, 824.24) * mm, "end": v(-749.12, 825.1) * mm});
            skLineSegment(sketch, "E303", {"start": v(-749.12, 825.1) * mm, "end": v(-748.93, 825.96) * mm});
            skLineSegment(sketch, "E304", {"start": v(-748.93, 825.96) * mm, "end": v(-748.71, 826.78) * mm});
            skLineSegment(sketch, "E305", {"start": v(-748.71, 826.78) * mm, "end": v(-748.5, 827.63) * mm});
            skLineSegment(sketch, "E306", {"start": v(-748.5, 827.63) * mm, "end": v(-748.26, 828.44) * mm});
            skLineSegment(sketch, "E307", {"start": v(-748.26, 828.44) * mm, "end": v(-748, 829.25) * mm});
            skLineSegment(sketch, "E308", {"start": v(-748, 829.25) * mm, "end": v(-747.74, 830.05) * mm});
            skLineSegment(sketch, "E309", {"start": v(-747.74, 830.05) * mm, "end": v(-747.48, 830.84) * mm});
            skLineSegment(sketch, "E310", {"start": v(-747.48, 830.84) * mm, "end": v(-747.18, 831.62) * mm});
            skLineSegment(sketch, "E311", {"start": v(-747.18, 831.62) * mm, "end": v(-746.88, 832.38) * mm});
            skLineSegment(sketch, "E312", {"start": v(-746.88, 832.38) * mm, "end": v(-746.56, 833.12) * mm});
            skLineSegment(sketch, "E313", {"start": v(-746.56, 833.12) * mm, "end": v(-746.23, 833.86) * mm});
            skLineSegment(sketch, "E314", {"start": v(-746.23, 833.86) * mm, "end": v(-745.87, 834.58) * mm});
            skLineSegment(sketch, "E315", {"start": v(-745.87, 834.58) * mm, "end": v(-745.52, 835.29) * mm});
            skLineSegment(sketch, "E316", {"start": v(-745.52, 835.29) * mm, "end": v(-745.13, 836) * mm});
            skLineSegment(sketch, "E317", {"start": v(-745.13, 836) * mm, "end": v(-744.75, 836.66) * mm});
            skLineSegment(sketch, "E318", {"start": v(-744.75, 836.66) * mm, "end": v(-744.34, 837.33) * mm});
            skLineSegment(sketch, "E319", {"start": v(-744.34, 837.33) * mm, "end": v(-743.92, 837.99) * mm});
            skLineSegment(sketch, "E320", {"start": v(-743.92, 837.99) * mm, "end": v(-743.48, 838.6) * mm});
            skLineSegment(sketch, "E321", {"start": v(-743.48, 838.6) * mm, "end": v(-743.07, 839.3) * mm});
            skLineSegment(sketch, "E322", {"start": v(-743.07, 839.3) * mm, "end": v(-732.43, 849.57) * mm});
            skLineSegment(sketch, "E323", {"start": v(-732.43, 849.57) * mm, "end": v(-743.39, 863.86) * mm});
            skLineSegment(sketch, "E324", {"start": v(-743.39, 863.86) * mm, "end": v(-756.09, 856.24) * mm});
            skLineSegment(sketch, "E325", {"start": v(-756.09, 856.24) * mm, "end": v(-756.83, 856.03) * mm});
            skLineSegment(sketch, "E326", {"start": v(-756.83, 856.03) * mm, "end": v(-757.55, 855.76) * mm});
            skLineSegment(sketch, "E327", {"start": v(-757.55, 855.76) * mm, "end": v(-758.3, 855.52) * mm});
            skLineSegment(sketch, "E328", {"start": v(-758.3, 855.52) * mm, "end": v(-759.03, 855.29) * mm});
            skLineSegment(sketch, "E329", {"start": v(-759.03, 855.29) * mm, "end": v(-759.8, 855.1) * mm});
            skLineSegment(sketch, "E330", {"start": v(-759.8, 855.1) * mm, "end": v(-760.57, 854.9) * mm});
            skLineSegment(sketch, "E331", {"start": v(-760.57, 854.9) * mm, "end": v(-761.34, 854.74) * mm});
            skLineSegment(sketch, "E332", {"start": v(-761.34, 854.74) * mm, "end": v(-762.14, 854.58) * mm});
            skLineSegment(sketch, "E333", {"start": v(-762.14, 854.58) * mm, "end": v(-762.93, 854.46) * mm});
            skLineSegment(sketch, "E334", {"start": v(-762.93, 854.46) * mm, "end": v(-763.74, 854.35) * mm});
            skLineSegment(sketch, "E335", {"start": v(-763.74, 854.35) * mm, "end": v(-764.55, 854.25) * mm});
            skLineSegment(sketch, "E336", {"start": v(-764.55, 854.25) * mm, "end": v(-765.38, 854.18) * mm});
            skLineSegment(sketch, "E337", {"start": v(-765.38, 854.18) * mm, "end": v(-766.21, 854.1) * mm});
            skLineSegment(sketch, "E338", {"start": v(-766.21, 854.1) * mm, "end": v(-767.04, 854.05) * mm});
            skLineSegment(sketch, "E339", {"start": v(-767.04, 854.05) * mm, "end": v(-767.89, 854.04) * mm});
            skLineSegment(sketch, "E340", {"start": v(-767.89, 854.04) * mm, "end": v(-768.75, 854.02) * mm});
            skLineSegment(sketch, "E341", {"start": v(-768.75, 854.02) * mm, "end": v(-769.6, 854.02) * mm});
            skLineSegment(sketch, "E342", {"start": v(-769.6, 854.02) * mm, "end": v(-770.48, 854.04) * mm});
            skLineSegment(sketch, "E343", {"start": v(-770.48, 854.04) * mm, "end": v(-771.34, 854.05) * mm});
            skLineSegment(sketch, "E344", {"start": v(-771.34, 854.05) * mm, "end": v(-772.23, 854.1) * mm});
            skLineSegment(sketch, "E345", {"start": v(-772.23, 854.1) * mm, "end": v(-773.1, 854.18) * mm});
            skLineSegment(sketch, "E346", {"start": v(-773.1, 854.18) * mm, "end": v(-774, 854.25) * mm});
            skLineSegment(sketch, "E347", {"start": v(-774, 854.25) * mm, "end": v(-774.89, 854.35) * mm});
            skLineSegment(sketch, "E348", {"start": v(-774.89, 854.35) * mm, "end": v(-775.8, 854.46) * mm});
            skLineSegment(sketch, "E349", {"start": v(-775.8, 854.46) * mm, "end": v(-776.7, 854.58) * mm});
            skLineSegment(sketch, "E350", {"start": v(-776.7, 854.58) * mm, "end": v(-777.62, 854.72) * mm});
            skLineSegment(sketch, "E351", {"start": v(-777.62, 854.72) * mm, "end": v(-778.54, 854.88) * mm});
            skLineSegment(sketch, "E352", {"start": v(-778.54, 854.88) * mm, "end": v(-779.46, 855.06) * mm});
            skLineSegment(sketch, "E353", {"start": v(-779.46, 855.06) * mm, "end": v(-780.4, 855.24) * mm});
            skLineSegment(sketch, "E354", {"start": v(-780.4, 855.24) * mm, "end": v(-781.31, 855.45) * mm});
            skLineSegment(sketch, "E355", {"start": v(-781.31, 855.45) * mm, "end": v(-783.29, 859.95) * mm});
            skLineSegment(sketch, "E356", {"start": v(-783.29, 859.95) * mm, "end": v(-785.09, 864.53) * mm});
            skLineSegment(sketch, "E357", {"start": v(-785.09, 864.53) * mm, "end": v(-784.57, 865.33) * mm});
            skLineSegment(sketch, "E358", {"start": v(-784.57, 865.33) * mm, "end": v(-784.04, 866.12) * mm});
            skLineSegment(sketch, "E359", {"start": v(-784.04, 866.12) * mm, "end": v(-783.52, 866.9) * mm});
            skLineSegment(sketch, "E360", {"start": v(-783.52, 866.9) * mm, "end": v(-782.97, 867.65) * mm});
            skLineSegment(sketch, "E361", {"start": v(-782.97, 867.65) * mm, "end": v(-782.44, 868.4) * mm});
            skLineSegment(sketch, "E362", {"start": v(-782.44, 868.4) * mm, "end": v(-781.87, 869.14) * mm});
            skLineSegment(sketch, "E363", {"start": v(-781.87, 869.14) * mm, "end": v(-781.31, 869.84) * mm});
            skLineSegment(sketch, "E364", {"start": v(-781.31, 869.84) * mm, "end": v(-780.75, 870.55) * mm});
            skLineSegment(sketch, "E365", {"start": v(-780.75, 870.55) * mm, "end": v(-780.18, 871.23) * mm});
            skLineSegment(sketch, "E366", {"start": v(-780.18, 871.23) * mm, "end": v(-779.6, 871.9) * mm});
            skLineSegment(sketch, "E367", {"start": v(-779.6, 871.9) * mm, "end": v(-779, 872.56) * mm});
            skLineSegment(sketch, "E368", {"start": v(-779, 872.56) * mm, "end": v(-778.42, 873.2) * mm});
            skLineSegment(sketch, "E369", {"start": v(-778.42, 873.2) * mm, "end": v(-777.82, 873.83) * mm});
            skLineSegment(sketch, "E370", {"start": v(-777.82, 873.83) * mm, "end": v(-777.2, 874.43) * mm});
            skLineSegment(sketch, "E371", {"start": v(-777.2, 874.43) * mm, "end": v(-776.58, 875.03) * mm});
            skLineSegment(sketch, "E372", {"start": v(-776.58, 875.03) * mm, "end": v(-775.97, 875.6) * mm});
            skLineSegment(sketch, "E373", {"start": v(-775.97, 875.6) * mm, "end": v(-775.35, 876.16) * mm});
            skLineSegment(sketch, "E374", {"start": v(-775.35, 876.16) * mm, "end": v(-774.71, 876.7) * mm});
            skLineSegment(sketch, "E375", {"start": v(-774.71, 876.7) * mm, "end": v(-774.08, 877.23) * mm});
            skLineSegment(sketch, "E376", {"start": v(-774.08, 877.23) * mm, "end": v(-773.43, 877.74) * mm});
            skLineSegment(sketch, "E377", {"start": v(-773.43, 877.74) * mm, "end": v(-772.77, 878.22) * mm});
            skLineSegment(sketch, "E378", {"start": v(-772.77, 878.22) * mm, "end": v(-772.12, 878.7) * mm});
            skLineSegment(sketch, "E379", {"start": v(-772.12, 878.7) * mm, "end": v(-771.45, 879.15) * mm});
            skLineSegment(sketch, "E380", {"start": v(-771.45, 879.15) * mm, "end": v(-770.78, 879.58) * mm});
            skLineSegment(sketch, "E381", {"start": v(-770.78, 879.58) * mm, "end": v(-770.1, 880) * mm});
            skLineSegment(sketch, "E382", {"start": v(-770.1, 880) * mm, "end": v(-769.44, 880.39) * mm});
            skLineSegment(sketch, "E383", {"start": v(-769.44, 880.39) * mm, "end": v(-768.75, 880.76) * mm});
            skLineSegment(sketch, "E384", {"start": v(-768.75, 880.76) * mm, "end": v(-768.06, 881.11) * mm});
            skLineSegment(sketch, "E385", {"start": v(-768.06, 881.11) * mm, "end": v(-767.36, 881.43) * mm});
            skLineSegment(sketch, "E386", {"start": v(-767.36, 881.43) * mm, "end": v(-766.67, 881.82) * mm});
            skLineSegment(sketch, "E387", {"start": v(-766.67, 881.82) * mm, "end": v(-752.31, 885.4) * mm});
            skLineSegment(sketch, "E388", {"start": v(-752.31, 885.4) * mm, "end": v(-754.66, 903.25) * mm});
            skLineSegment(sketch, "E389", {"start": v(-754.66, 903.25) * mm, "end": v(-769.46, 903) * mm});
            skLineSegment(sketch, "E390", {"start": v(-769.46, 903) * mm, "end": v(-770.22, 903.2) * mm});
            skLineSegment(sketch, "E391", {"start": v(-770.22, 903.2) * mm, "end": v(-770.97, 903.34) * mm});
            skLineSegment(sketch, "E392", {"start": v(-770.97, 903.34) * mm, "end": v(-771.73, 903.48) * mm});
            skLineSegment(sketch, "E393", {"start": v(-771.73, 903.48) * mm, "end": v(-772.5, 903.67) * mm});
            skLineSegment(sketch, "E394", {"start": v(-772.5, 903.67) * mm, "end": v(-773.25, 903.87) * mm});
            skLineSegment(sketch, "E395", {"start": v(-773.25, 903.87) * mm, "end": v(-774, 904.1) * mm});
            skLineSegment(sketch, "E396", {"start": v(-774, 904.1) * mm, "end": v(-774.77, 904.34) * mm});
            skLineSegment(sketch, "E397", {"start": v(-774.77, 904.34) * mm, "end": v(-775.52, 904.6) * mm});
            skLineSegment(sketch, "E398", {"start": v(-775.52, 904.6) * mm, "end": v(-776.28, 904.89) * mm});
            skLineSegment(sketch, "E399", {"start": v(-776.28, 904.89) * mm, "end": v(-777.04, 905.19) * mm});
            skLineSegment(sketch, "E400", {"start": v(-777.04, 905.19) * mm, "end": v(-777.8, 905.52) * mm});
            skLineSegment(sketch, "E401", {"start": v(-777.8, 905.52) * mm, "end": v(-778.54, 905.86) * mm});
            skLineSegment(sketch, "E402", {"start": v(-778.54, 905.86) * mm, "end": v(-779.3, 906.23) * mm});
            skLineSegment(sketch, "E403", {"start": v(-779.3, 906.23) * mm, "end": v(-780.06, 906.6) * mm});
            skLineSegment(sketch, "E404", {"start": v(-780.06, 906.6) * mm, "end": v(-780.8, 906.99) * mm});
            skLineSegment(sketch, "E405", {"start": v(-780.8, 906.99) * mm, "end": v(-781.54, 907.41) * mm});
            skLineSegment(sketch, "E406", {"start": v(-781.54, 907.41) * mm, "end": v(-782.3, 907.84) * mm});
            skLineSegment(sketch, "E407", {"start": v(-782.3, 907.84) * mm, "end": v(-783.04, 908.3) * mm});
            skLineSegment(sketch, "E408", {"start": v(-783.04, 908.3) * mm, "end": v(-783.78, 908.75) * mm});
            skLineSegment(sketch, "E409", {"start": v(-783.78, 908.75) * mm, "end": v(-784.5, 909.23) * mm});
            skLineSegment(sketch, "E410", {"start": v(-784.5, 909.23) * mm, "end": v(-785.24, 909.72) * mm});
            skLineSegment(sketch, "E411", {"start": v(-785.24, 909.72) * mm, "end": v(-785.98, 910.25) * mm});
            skLineSegment(sketch, "E412", {"start": v(-785.98, 910.25) * mm, "end": v(-786.7, 910.78) * mm});
            skLineSegment(sketch, "E413", {"start": v(-786.7, 910.78) * mm, "end": v(-787.43, 911.33) * mm});
            skLineSegment(sketch, "E414", {"start": v(-787.43, 911.33) * mm, "end": v(-788.15, 911.9) * mm});
            skLineSegment(sketch, "E415", {"start": v(-788.15, 911.9) * mm, "end": v(-788.88, 912.46) * mm});
            skLineSegment(sketch, "E416", {"start": v(-788.88, 912.46) * mm, "end": v(-789.58, 913.06) * mm});
            skLineSegment(sketch, "E417", {"start": v(-789.58, 913.06) * mm, "end": v(-790.3, 913.67) * mm});
            skLineSegment(sketch, "E418", {"start": v(-790.3, 913.67) * mm, "end": v(-791.01, 914.3) * mm});
            skLineSegment(sketch, "E419", {"start": v(-791.01, 914.3) * mm, "end": v(-791.72, 914.93) * mm});
            skLineSegment(sketch, "E420", {"start": v(-791.72, 914.93) * mm, "end": v(-791.17, 919.83) * mm});
            skLineSegment(sketch, "E421", {"start": v(-791.17, 919.83) * mm, "end": v(-790.43, 924.68) * mm});
            skLineSegment(sketch, "E422", {"start": v(-790.43, 924.68) * mm, "end": v(-789.58, 925.12) * mm});
            skLineSegment(sketch, "E423", {"start": v(-789.58, 925.12) * mm, "end": v(-788.74, 925.54) * mm});
            skLineSegment(sketch, "E424", {"start": v(-788.74, 925.54) * mm, "end": v(-787.89, 925.95) * mm});
            skLineSegment(sketch, "E425", {"start": v(-787.89, 925.95) * mm, "end": v(-787.04, 926.34) * mm});
            skLineSegment(sketch, "E426", {"start": v(-787.04, 926.34) * mm, "end": v(-786.2, 926.7) * mm});
            skLineSegment(sketch, "E427", {"start": v(-786.2, 926.7) * mm, "end": v(-785.37, 927.06) * mm});
            skLineSegment(sketch, "E428", {"start": v(-785.37, 927.06) * mm, "end": v(-784.52, 927.41) * mm});
            skLineSegment(sketch, "E429", {"start": v(-784.52, 927.41) * mm, "end": v(-783.67, 927.73) * mm});
            skLineSegment(sketch, "E430", {"start": v(-783.67, 927.73) * mm, "end": v(-782.83, 928.03) * mm});
            skLineSegment(sketch, "E431", {"start": v(-782.83, 928.03) * mm, "end": v(-782, 928.33) * mm});
            skLineSegment(sketch, "E432", {"start": v(-782, 928.33) * mm, "end": v(-781.15, 928.6) * mm});
            skLineSegment(sketch, "E433", {"start": v(-781.15, 928.6) * mm, "end": v(-780.32, 928.86) * mm});
            skLineSegment(sketch, "E434", {"start": v(-780.32, 928.86) * mm, "end": v(-779.5, 929.1) * mm});
            skLineSegment(sketch, "E435", {"start": v(-779.5, 929.1) * mm, "end": v(-778.66, 929.32) * mm});
            skLineSegment(sketch, "E436", {"start": v(-778.66, 929.32) * mm, "end": v(-777.84, 929.53) * mm});
            skLineSegment(sketch, "E437", {"start": v(-777.84, 929.53) * mm, "end": v(-777, 929.72) * mm});
            skLineSegment(sketch, "E438", {"start": v(-777, 929.72) * mm, "end": v(-776.18, 929.88) * mm});
            skLineSegment(sketch, "E439", {"start": v(-776.18, 929.88) * mm, "end": v(-775.37, 930.04) * mm});
            skLineSegment(sketch, "E440", {"start": v(-775.37, 930.04) * mm, "end": v(-774.55, 930.18) * mm});
            skLineSegment(sketch, "E441", {"start": v(-774.55, 930.18) * mm, "end": v(-773.74, 930.29) * mm});
            skLineSegment(sketch, "E442", {"start": v(-773.74, 930.29) * mm, "end": v(-772.93, 930.4) * mm});
            skLineSegment(sketch, "E443", {"start": v(-772.93, 930.4) * mm, "end": v(-772.12, 930.48) * mm});
            skLineSegment(sketch, "E444", {"start": v(-772.12, 930.48) * mm, "end": v(-771.33, 930.54) * mm});
            skLineSegment(sketch, "E445", {"start": v(-771.33, 930.54) * mm, "end": v(-770.53, 930.57) * mm});
            skLineSegment(sketch, "E446", {"start": v(-770.53, 930.57) * mm, "end": v(-769.74, 930.6) * mm});
            skLineSegment(sketch, "E447", {"start": v(-769.74, 930.6) * mm, "end": v(-768.95, 930.6) * mm});
            skLineSegment(sketch, "E448", {"start": v(-768.95, 930.6) * mm, "end": v(-768.17, 930.57) * mm});
            skLineSegment(sketch, "E449", {"start": v(-768.17, 930.57) * mm, "end": v(-767.4, 930.54) * mm});
            skLineSegment(sketch, "E450", {"start": v(-767.4, 930.54) * mm, "end": v(-766.63, 930.47) * mm});
            skLineSegment(sketch, "E451", {"start": v(-766.63, 930.47) * mm, "end": v(-765.84, 930.45) * mm});
            skLineSegment(sketch, "E452", {"start": v(-765.84, 930.45) * mm, "end": v(-751.62, 926.37) * mm});
            skLineSegment(sketch, "E453", {"start": v(-751.62, 926.37) * mm, "end": v(-744.73, 943) * mm});
            skLineSegment(sketch, "E454", {"start": v(-744.73, 943) * mm, "end": v(-757.67, 950.2) * mm});
            skLineSegment(sketch, "E455", {"start": v(-757.67, 950.2) * mm, "end": v(-758.24, 950.75) * mm});
            skLineSegment(sketch, "E456", {"start": v(-758.24, 950.75) * mm, "end": v(-758.82, 951.24) * mm});
            skLineSegment(sketch, "E457", {"start": v(-758.82, 951.24) * mm, "end": v(-759.4, 951.76) * mm});
            skLineSegment(sketch, "E458", {"start": v(-759.4, 951.76) * mm, "end": v(-759.97, 952.28) * mm});
            skLineSegment(sketch, "E459", {"start": v(-759.97, 952.28) * mm, "end": v(-760.53, 952.85) * mm});
            skLineSegment(sketch, "E460", {"start": v(-760.53, 952.85) * mm, "end": v(-761.06, 953.41) * mm});
            skLineSegment(sketch, "E461", {"start": v(-761.06, 953.41) * mm, "end": v(-761.6, 954.01) * mm});
            skLineSegment(sketch, "E462", {"start": v(-761.6, 954.01) * mm, "end": v(-762.12, 954.61) * mm});
            skLineSegment(sketch, "E463", {"start": v(-762.12, 954.61) * mm, "end": v(-762.63, 955.25) * mm});
            skLineSegment(sketch, "E464", {"start": v(-762.63, 955.25) * mm, "end": v(-763.14, 955.88) * mm});
            skLineSegment(sketch, "E465", {"start": v(-763.14, 955.88) * mm, "end": v(-763.64, 956.54) * mm});
            skLineSegment(sketch, "E466", {"start": v(-763.64, 956.54) * mm, "end": v(-764.11, 957.2) * mm});
            skLineSegment(sketch, "E467", {"start": v(-764.11, 957.2) * mm, "end": v(-764.59, 957.9) * mm});
            skLineSegment(sketch, "E468", {"start": v(-764.59, 957.9) * mm, "end": v(-765.05, 958.6) * mm});
            skLineSegment(sketch, "E469", {"start": v(-765.05, 958.6) * mm, "end": v(-765.49, 959.32) * mm});
            skLineSegment(sketch, "E470", {"start": v(-765.49, 959.32) * mm, "end": v(-765.93, 960.05) * mm});
            skLineSegment(sketch, "E471", {"start": v(-765.93, 960.05) * mm, "end": v(-766.35, 960.8) * mm});
            skLineSegment(sketch, "E472", {"start": v(-766.35, 960.8) * mm, "end": v(-766.78, 961.56) * mm});
            skLineSegment(sketch, "E473", {"start": v(-766.78, 961.56) * mm, "end": v(-767.18, 962.32) * mm});
            skLineSegment(sketch, "E474", {"start": v(-767.18, 962.32) * mm, "end": v(-767.59, 963.12) * mm});
            skLineSegment(sketch, "E475", {"start": v(-767.59, 963.12) * mm, "end": v(-767.98, 963.9) * mm});
            skLineSegment(sketch, "E476", {"start": v(-767.98, 963.9) * mm, "end": v(-768.35, 964.72) * mm});
            skLineSegment(sketch, "E477", {"start": v(-768.35, 964.72) * mm, "end": v(-768.72, 965.55) * mm});
            skLineSegment(sketch, "E478", {"start": v(-768.72, 965.55) * mm, "end": v(-769.07, 966.38) * mm});
            skLineSegment(sketch, "E479", {"start": v(-769.07, 966.38) * mm, "end": v(-769.42, 967.22) * mm});
            skLineSegment(sketch, "E480", {"start": v(-769.42, 967.22) * mm, "end": v(-769.76, 968.09) * mm});
            skLineSegment(sketch, "E481", {"start": v(-769.76, 968.09) * mm, "end": v(-770.07, 968.97) * mm});
            skLineSegment(sketch, "E482", {"start": v(-770.07, 968.97) * mm, "end": v(-770.4, 969.85) * mm});
            skLineSegment(sketch, "E483", {"start": v(-770.4, 969.85) * mm, "end": v(-770.7, 970.75) * mm});
            skLineSegment(sketch, "E484", {"start": v(-770.7, 970.75) * mm, "end": v(-770.97, 971.65) * mm});
            skLineSegment(sketch, "E485", {"start": v(-770.97, 971.65) * mm, "end": v(-768.06, 975.62) * mm});
            skLineSegment(sketch, "E486", {"start": v(-768.06, 975.62) * mm, "end": v(-765, 979.47) * mm});
            skLineSegment(sketch, "E487", {"start": v(-765, 979.47) * mm, "end": v(-764.04, 979.41) * mm});
            skLineSegment(sketch, "E488", {"start": v(-764.04, 979.41) * mm, "end": v(-763.09, 979.36) * mm});
            skLineSegment(sketch, "E489", {"start": v(-763.09, 979.36) * mm, "end": v(-762.15, 979.3) * mm});
            skLineSegment(sketch, "E490", {"start": v(-762.15, 979.3) * mm, "end": v(-761.24, 979.2) * mm});
            skLineSegment(sketch, "E491", {"start": v(-761.24, 979.2) * mm, "end": v(-760.32, 979.1) * mm});
            skLineSegment(sketch, "E492", {"start": v(-760.32, 979.1) * mm, "end": v(-759.4, 979) * mm});
            skLineSegment(sketch, "E493", {"start": v(-759.4, 979) * mm, "end": v(-758.5, 978.87) * mm});
            skLineSegment(sketch, "E494", {"start": v(-758.5, 978.87) * mm, "end": v(-757.62, 978.73) * mm});
            skLineSegment(sketch, "E495", {"start": v(-757.62, 978.73) * mm, "end": v(-756.74, 978.57) * mm});
            skLineSegment(sketch, "E496", {"start": v(-756.74, 978.57) * mm, "end": v(-755.86, 978.39) * mm});
            skLineSegment(sketch, "E497", {"start": v(-755.86, 978.39) * mm, "end": v(-755, 978.21) * mm});
            skLineSegment(sketch, "E498", {"start": v(-755, 978.21) * mm, "end": v(-754.15, 978.02) * mm});
            skLineSegment(sketch, "E499", {"start": v(-754.15, 978.02) * mm, "end": v(-753.3, 977.8) * mm});
            skLineSegment(sketch, "E500", {"start": v(-753.3, 977.8) * mm, "end": v(-752.47, 977.6) * mm});
            skLineSegment(sketch, "E501", {"start": v(-752.47, 977.6) * mm, "end": v(-751.66, 977.35) * mm});
            skLineSegment(sketch, "E502", {"start": v(-751.66, 977.35) * mm, "end": v(-750.85, 977.1) * mm});
            skLineSegment(sketch, "E503", {"start": v(-750.85, 977.1) * mm, "end": v(-750.05, 976.84) * mm});
            skLineSegment(sketch, "E504", {"start": v(-750.05, 976.84) * mm, "end": v(-749.26, 976.56) * mm});
            skLineSegment(sketch, "E505", {"start": v(-749.26, 976.56) * mm, "end": v(-748.48, 976.27) * mm});
            skLineSegment(sketch, "E506", {"start": v(-748.48, 976.27) * mm, "end": v(-747.73, 975.97) * mm});
            skLineSegment(sketch, "E507", {"start": v(-747.73, 975.97) * mm, "end": v(-746.97, 975.66) * mm});
            skLineSegment(sketch, "E508", {"start": v(-746.97, 975.66) * mm, "end": v(-746.24, 975.32) * mm});
            skLineSegment(sketch, "E509", {"start": v(-746.24, 975.32) * mm, "end": v(-745.52, 974.97) * mm});
            skLineSegment(sketch, "E510", {"start": v(-745.52, 974.97) * mm, "end": v(-744.8, 974.62) * mm});
            skLineSegment(sketch, "E511", {"start": v(-744.8, 974.62) * mm, "end": v(-744.11, 974.23) * mm});
            skLineSegment(sketch, "E512", {"start": v(-744.11, 974.23) * mm, "end": v(-743.44, 973.84) * mm});
            skLineSegment(sketch, "E513", {"start": v(-743.44, 973.84) * mm, "end": v(-742.77, 973.43) * mm});
            skLineSegment(sketch, "E514", {"start": v(-742.77, 973.43) * mm, "end": v(-742.12, 973.01) * mm});
            skLineSegment(sketch, "E515", {"start": v(-742.12, 973.01) * mm, "end": v(-741.48, 972.57) * mm});
            skLineSegment(sketch, "E516", {"start": v(-741.48, 972.57) * mm, "end": v(-740.81, 972.16) * mm});
            skLineSegment(sketch, "E517", {"start": v(-740.81, 972.16) * mm, "end": v(-730.53, 961.51) * mm});
            skLineSegment(sketch, "E518", {"start": v(-730.53, 961.51) * mm, "end": v(-716.24, 972.48) * mm});
            skLineSegment(sketch, "E519", {"start": v(-716.24, 972.48) * mm, "end": v(-723.86, 985.16) * mm});
            skLineSegment(sketch, "E520", {"start": v(-723.86, 985.16) * mm, "end": v(-724.07, 985.92) * mm});
            skLineSegment(sketch, "E521", {"start": v(-724.07, 985.92) * mm, "end": v(-724.34, 986.64) * mm});
            skLineSegment(sketch, "E522", {"start": v(-724.34, 986.64) * mm, "end": v(-724.58, 987.39) * mm});
            skLineSegment(sketch, "E523", {"start": v(-724.58, 987.39) * mm, "end": v(-724.81, 988.13) * mm});
            skLineSegment(sketch, "E524", {"start": v(-724.81, 988.13) * mm, "end": v(-725, 988.89) * mm});
            skLineSegment(sketch, "E525", {"start": v(-725, 988.89) * mm, "end": v(-725.2, 989.66) * mm});
            skLineSegment(sketch, "E526", {"start": v(-725.2, 989.66) * mm, "end": v(-725.36, 990.44) * mm});
            skLineSegment(sketch, "E527", {"start": v(-725.36, 990.44) * mm, "end": v(-725.52, 991.23) * mm});
            skLineSegment(sketch, "E528", {"start": v(-725.52, 991.23) * mm, "end": v(-725.64, 992.03) * mm});
            skLineSegment(sketch, "E529", {"start": v(-725.64, 992.03) * mm, "end": v(-725.75, 992.84) * mm});
            skLineSegment(sketch, "E530", {"start": v(-725.75, 992.84) * mm, "end": v(-725.85, 993.65) * mm});
            skLineSegment(sketch, "E531", {"start": v(-725.85, 993.65) * mm, "end": v(-725.92, 994.46) * mm});
            skLineSegment(sketch, "E532", {"start": v(-725.92, 994.46) * mm, "end": v(-726, 995.3) * mm});
            skLineSegment(sketch, "E533", {"start": v(-726, 995.3) * mm, "end": v(-726.05, 996.14) * mm});
            skLineSegment(sketch, "E534", {"start": v(-726.05, 996.14) * mm, "end": v(-726.07, 996.98) * mm});
            skLineSegment(sketch, "E535", {"start": v(-726.07, 996.98) * mm, "end": v(-726.08, 997.83) * mm});
            skLineSegment(sketch, "E536", {"start": v(-726.08, 997.83) * mm, "end": v(-726.08, 998.7) * mm});
            skLineSegment(sketch, "E537", {"start": v(-726.08, 998.7) * mm, "end": v(-726.07, 999.56) * mm});
            skLineSegment(sketch, "E538", {"start": v(-726.07, 999.56) * mm, "end": v(-726.03, 1000.44) * mm});
            skLineSegment(sketch, "E539", {"start": v(-726.03, 1000.44) * mm, "end": v(-726, 1001.32) * mm});
            skLineSegment(sketch, "E540", {"start": v(-726, 1001.32) * mm, "end": v(-725.92, 1002.2) * mm});
            skLineSegment(sketch, "E541", {"start": v(-725.92, 1002.2) * mm, "end": v(-725.85, 1003.09) * mm});
            skLineSegment(sketch, "E542", {"start": v(-725.85, 1003.09) * mm, "end": v(-725.75, 1003.98) * mm});
            skLineSegment(sketch, "E543", {"start": v(-725.75, 1003.98) * mm, "end": v(-725.64, 1004.88) * mm});
            skLineSegment(sketch, "E544", {"start": v(-725.64, 1004.88) * mm, "end": v(-725.52, 1005.8) * mm});
            skLineSegment(sketch, "E545", {"start": v(-725.52, 1005.8) * mm, "end": v(-725.38, 1006.72) * mm});
            skLineSegment(sketch, "E546", {"start": v(-725.38, 1006.72) * mm, "end": v(-725.22, 1007.64) * mm});
            skLineSegment(sketch, "E547", {"start": v(-725.22, 1007.64) * mm, "end": v(-725.04, 1008.55) * mm});
            skLineSegment(sketch, "E548", {"start": v(-725.04, 1008.55) * mm, "end": v(-724.87, 1009.47) * mm});
            skLineSegment(sketch, "E549", {"start": v(-724.87, 1009.47) * mm, "end": v(-724.65, 1010.4) * mm});
            skLineSegment(sketch, "E550", {"start": v(-724.65, 1010.4) * mm, "end": v(-720.16, 1012.38) * mm});
            skLineSegment(sketch, "E551", {"start": v(-720.16, 1012.38) * mm, "end": v(-715.57, 1014.18) * mm});
            skLineSegment(sketch, "E552", {"start": v(-715.57, 1014.18) * mm, "end": v(-714.76, 1013.65) * mm});
            skLineSegment(sketch, "E553", {"start": v(-714.76, 1013.65) * mm, "end": v(-713.98, 1013.14) * mm});
            skLineSegment(sketch, "E554", {"start": v(-713.98, 1013.14) * mm, "end": v(-713.2, 1012.61) * mm});
            skLineSegment(sketch, "E555", {"start": v(-713.2, 1012.61) * mm, "end": v(-712.45, 1012.06) * mm});
            skLineSegment(sketch, "E556", {"start": v(-712.45, 1012.06) * mm, "end": v(-711.7, 1011.52) * mm});
            skLineSegment(sketch, "E557", {"start": v(-711.7, 1011.52) * mm, "end": v(-710.97, 1010.97) * mm});
            skLineSegment(sketch, "E558", {"start": v(-710.97, 1010.97) * mm, "end": v(-710.26, 1010.4) * mm});
            skLineSegment(sketch, "E559", {"start": v(-710.26, 1010.4) * mm, "end": v(-709.56, 1009.84) * mm});
            skLineSegment(sketch, "E560", {"start": v(-709.56, 1009.84) * mm, "end": v(-708.87, 1009.28) * mm});
            skLineSegment(sketch, "E561", {"start": v(-708.87, 1009.28) * mm, "end": v(-708.2, 1008.7) * mm});
            skLineSegment(sketch, "E562", {"start": v(-708.2, 1008.7) * mm, "end": v(-707.54, 1008.1) * mm});
            skLineSegment(sketch, "E563", {"start": v(-707.54, 1008.1) * mm, "end": v(-706.9, 1007.51) * mm});
            skLineSegment(sketch, "E564", {"start": v(-706.9, 1007.51) * mm, "end": v(-706.27, 1006.9) * mm});
            skLineSegment(sketch, "E565", {"start": v(-706.27, 1006.9) * mm, "end": v(-705.67, 1006.3) * mm});
            skLineSegment(sketch, "E566", {"start": v(-705.67, 1006.3) * mm, "end": v(-705.08, 1005.68) * mm});
            skLineSegment(sketch, "E567", {"start": v(-705.08, 1005.68) * mm, "end": v(-704.5, 1005.06) * mm});
            skLineSegment(sketch, "E568", {"start": v(-704.5, 1005.06) * mm, "end": v(-703.95, 1004.43) * mm});
            skLineSegment(sketch, "E569", {"start": v(-703.95, 1004.43) * mm, "end": v(-703.4, 1003.8) * mm});
            skLineSegment(sketch, "E570", {"start": v(-703.4, 1003.8) * mm, "end": v(-702.87, 1003.16) * mm});
            skLineSegment(sketch, "E571", {"start": v(-702.87, 1003.16) * mm, "end": v(-702.36, 1002.52) * mm});
            skLineSegment(sketch, "E572", {"start": v(-702.36, 1002.52) * mm, "end": v(-701.86, 1001.87) * mm});
            skLineSegment(sketch, "E573", {"start": v(-701.86, 1001.87) * mm, "end": v(-701.4, 1001.22) * mm});
            skLineSegment(sketch, "E574", {"start": v(-701.4, 1001.22) * mm, "end": v(-700.95, 1000.55) * mm});
            skLineSegment(sketch, "E575", {"start": v(-700.95, 1000.55) * mm, "end": v(-700.5, 999.88) * mm});
            skLineSegment(sketch, "E576", {"start": v(-700.5, 999.88) * mm, "end": v(-700.1, 999.2) * mm});
            skLineSegment(sketch, "E577", {"start": v(-700.1, 999.2) * mm, "end": v(-699.71, 998.53) * mm});
            skLineSegment(sketch, "E578", {"start": v(-699.71, 998.53) * mm, "end": v(-699.34, 997.85) * mm});
            skLineSegment(sketch, "E579", {"start": v(-699.34, 997.85) * mm, "end": v(-698.99, 997.14) * mm});
            skLineSegment(sketch, "E580", {"start": v(-698.99, 997.14) * mm, "end": v(-698.67, 996.45) * mm});
            skLineSegment(sketch, "E581", {"start": v(-698.67, 996.45) * mm, "end": v(-698.28, 995.76) * mm});
            skLineSegment(sketch, "E582", {"start": v(-698.28, 995.76) * mm, "end": v(-694.7, 981.4) * mm});
            skLineSegment(sketch, "E583", {"start": v(-694.7, 981.4) * mm, "end": v(-676.85, 983.75) * mm});
            skLineSegment(sketch, "E584", {"start": v(-676.85, 983.75) * mm, "end": v(-677.1, 998.55) * mm});
            skLineSegment(sketch, "E585", {"start": v(-677.1, 998.55) * mm, "end": v(-676.9, 999.3) * mm});
            skLineSegment(sketch, "E586", {"start": v(-676.9, 999.3) * mm, "end": v(-676.76, 1000.07) * mm});
            skLineSegment(sketch, "E587", {"start": v(-676.76, 1000.07) * mm, "end": v(-676.6, 1000.83) * mm});
            skLineSegment(sketch, "E588", {"start": v(-676.6, 1000.83) * mm, "end": v(-676.43, 1001.59) * mm});
            skLineSegment(sketch, "E589", {"start": v(-676.43, 1001.59) * mm, "end": v(-676.24, 1002.34) * mm});
            skLineSegment(sketch, "E590", {"start": v(-676.24, 1002.34) * mm, "end": v(-676, 1003.1) * mm});
            skLineSegment(sketch, "E591", {"start": v(-676, 1003.1) * mm, "end": v(-675.76, 1003.86) * mm});
            skLineSegment(sketch, "E592", {"start": v(-675.76, 1003.86) * mm, "end": v(-675.5, 1004.62) * mm});
            skLineSegment(sketch, "E593", {"start": v(-675.5, 1004.62) * mm, "end": v(-675.21, 1005.38) * mm});
            skLineSegment(sketch, "E594", {"start": v(-675.21, 1005.38) * mm, "end": v(-674.91, 1006.14) * mm});
            skLineSegment(sketch, "E595", {"start": v(-674.91, 1006.14) * mm, "end": v(-674.58, 1006.9) * mm});
            skLineSegment(sketch, "E596", {"start": v(-674.58, 1006.9) * mm, "end": v(-674.24, 1007.64) * mm});
            skLineSegment(sketch, "E597", {"start": v(-674.24, 1007.64) * mm, "end": v(-673.87, 1008.4) * mm});
            skLineSegment(sketch, "E598", {"start": v(-673.87, 1008.4) * mm, "end": v(-673.5, 1009.14) * mm});
            skLineSegment(sketch, "E599", {"start": v(-673.5, 1009.14) * mm, "end": v(-673.1, 1009.9) * mm});
            skLineSegment(sketch, "E600", {"start": v(-673.1, 1009.9) * mm, "end": v(-672.7, 1010.63) * mm});
            skLineSegment(sketch, "E601", {"start": v(-672.7, 1010.63) * mm, "end": v(-672.27, 1011.37) * mm});
            skLineSegment(sketch, "E602", {"start": v(-672.27, 1011.37) * mm, "end": v(-671.8, 1012.12) * mm});
            skLineSegment(sketch, "E603", {"start": v(-671.8, 1012.12) * mm, "end": v(-671.35, 1012.86) * mm});
            skLineSegment(sketch, "E604", {"start": v(-671.35, 1012.86) * mm, "end": v(-670.87, 1013.6) * mm});
            skLineSegment(sketch, "E605", {"start": v(-670.87, 1013.6) * mm, "end": v(-670.36, 1014.34) * mm});
            skLineSegment(sketch, "E606", {"start": v(-670.36, 1014.34) * mm, "end": v(-669.85, 1015.06) * mm});
            skLineSegment(sketch, "E607", {"start": v(-669.85, 1015.06) * mm, "end": v(-669.32, 1015.8) * mm});
            skLineSegment(sketch, "E608", {"start": v(-669.32, 1015.8) * mm, "end": v(-668.77, 1016.53) * mm});
            skLineSegment(sketch, "E609", {"start": v(-668.77, 1016.53) * mm, "end": v(-668.2, 1017.25) * mm});
            skLineSegment(sketch, "E610", {"start": v(-668.2, 1017.25) * mm, "end": v(-667.65, 1017.97) * mm});
            skLineSegment(sketch, "E611", {"start": v(-667.65, 1017.97) * mm, "end": v(-667.05, 1018.68) * mm});
            skLineSegment(sketch, "E612", {"start": v(-667.05, 1018.68) * mm, "end": v(-666.43, 1019.4) * mm});
            skLineSegment(sketch, "E613", {"start": v(-666.43, 1019.4) * mm, "end": v(-665.81, 1020.1) * mm});
            skLineSegment(sketch, "E614", {"start": v(-665.81, 1020.1) * mm, "end": v(-665.16, 1020.81) * mm});
            skLineSegment(sketch, "E615", {"start": v(-665.16, 1020.81) * mm, "end": v(-660.27, 1020.26) * mm});
            skLineSegment(sketch, "E616", {"start": v(-660.27, 1020.26) * mm, "end": v(-655.4, 1019.52) * mm});
            skLineSegment(sketch, "E617", {"start": v(-655.4, 1019.52) * mm, "end": v(-654.98, 1018.68) * mm});
            skLineSegment(sketch, "E618", {"start": v(-654.98, 1018.68) * mm, "end": v(-654.56, 1017.83) * mm});
            skLineSegment(sketch, "E619", {"start": v(-654.56, 1017.83) * mm, "end": v(-654.15, 1016.98) * mm});
            skLineSegment(sketch, "E620", {"start": v(-654.15, 1016.98) * mm, "end": v(-653.76, 1016.14) * mm});
            skLineSegment(sketch, "E621", {"start": v(-653.76, 1016.14) * mm, "end": v(-653.4, 1015.3) * mm});
            skLineSegment(sketch, "E622", {"start": v(-653.4, 1015.3) * mm, "end": v(-653.02, 1014.44) * mm});
            skLineSegment(sketch, "E623", {"start": v(-653.02, 1014.44) * mm, "end": v(-652.69, 1013.62) * mm});
            skLineSegment(sketch, "E624", {"start": v(-652.69, 1013.62) * mm, "end": v(-652.37, 1012.77) * mm});
            skLineSegment(sketch, "E625", {"start": v(-652.37, 1012.77) * mm, "end": v(-652.05, 1011.92) * mm});
            skLineSegment(sketch, "E626", {"start": v(-652.05, 1011.92) * mm, "end": v(-651.77, 1011.1) * mm});
            skLineSegment(sketch, "E627", {"start": v(-651.77, 1011.1) * mm, "end": v(-651.5, 1010.25) * mm});
            skLineSegment(sketch, "E628", {"start": v(-651.5, 1010.25) * mm, "end": v(-651.24, 1009.42) * mm});
            skLineSegment(sketch, "E629", {"start": v(-651.24, 1009.42) * mm, "end": v(-651, 1008.59) * mm});
            skLineSegment(sketch, "E630", {"start": v(-651, 1008.59) * mm, "end": v(-650.78, 1007.76) * mm});
            skLineSegment(sketch, "E631", {"start": v(-650.78, 1007.76) * mm, "end": v(-650.57, 1006.93) * mm});
            skLineSegment(sketch, "E632", {"start": v(-650.57, 1006.93) * mm, "end": v(-650.38, 1006.1) * mm});
            skLineSegment(sketch, "E633", {"start": v(-650.38, 1006.1) * mm, "end": v(-650.22, 1005.27) * mm});
            skLineSegment(sketch, "E634", {"start": v(-650.22, 1005.27) * mm, "end": v(-650.06, 1004.46) * mm});
            skLineSegment(sketch, "E635", {"start": v(-650.06, 1004.46) * mm, "end": v(-649.92, 1003.63) * mm});
            skLineSegment(sketch, "E636", {"start": v(-649.92, 1003.63) * mm, "end": v(-649.8, 1002.82) * mm});
            skLineSegment(sketch, "E637", {"start": v(-649.8, 1002.82) * mm, "end": v(-649.7, 1002.03) * mm});
            skLineSegment(sketch, "E638", {"start": v(-649.7, 1002.03) * mm, "end": v(-649.62, 1001.22) * mm});
            skLineSegment(sketch, "E639", {"start": v(-649.62, 1001.22) * mm, "end": v(-649.57, 1000.42) * mm});
            skLineSegment(sketch, "E640", {"start": v(-649.57, 1000.42) * mm, "end": v(-649.51, 999.63) * mm});
            skLineSegment(sketch, "E641", {"start": v(-649.51, 999.63) * mm, "end": v(-649.5, 998.83) * mm});
            skLineSegment(sketch, "E642", {"start": v(-649.5, 998.83) * mm, "end": v(-649.5, 998.04) * mm});
            skLineSegment(sketch, "E643", {"start": v(-649.5, 998.04) * mm, "end": v(-649.53, 997.26) * mm});
            skLineSegment(sketch, "E644", {"start": v(-649.53, 997.26) * mm, "end": v(-649.57, 996.49) * mm});
            skLineSegment(sketch, "E645", {"start": v(-649.57, 996.49) * mm, "end": v(-649.64, 995.73) * mm});
            skLineSegment(sketch, "E646", {"start": v(-649.64, 995.73) * mm, "end": v(-649.65, 994.94) * mm});
            skLineSegment(sketch, "E647", {"start": v(-649.65, 994.94) * mm, "end": v(-653.73, 980.7) * mm});
            skLineSegment(sketch, "E648", {"start": v(-653.73, 980.7) * mm, "end": v(-637.1, 973.82) * mm});
            skLineSegment(sketch, "E649", {"start": v(-637.1, 973.82) * mm, "end": v(-629.9, 986.77) * mm});
            skLineSegment(sketch, "E650", {"start": v(-629.9, 986.77) * mm, "end": v(-629.35, 987.33) * mm});
            skLineSegment(sketch, "E651", {"start": v(-629.35, 987.33) * mm, "end": v(-628.86, 987.91) * mm});
            skLineSegment(sketch, "E652", {"start": v(-628.86, 987.91) * mm, "end": v(-628.35, 988.5) * mm});
            skLineSegment(sketch, "E653", {"start": v(-628.35, 988.5) * mm, "end": v(-627.82, 989.06) * mm});
            skLineSegment(sketch, "E654", {"start": v(-627.82, 989.06) * mm, "end": v(-627.25, 989.6) * mm});
            skLineSegment(sketch, "E655", {"start": v(-627.25, 989.6) * mm, "end": v(-626.69, 990.16) * mm});
            skLineSegment(sketch, "E656", {"start": v(-626.69, 990.16) * mm, "end": v(-626.09, 990.7) * mm});
            skLineSegment(sketch, "E657", {"start": v(-626.09, 990.7) * mm, "end": v(-625.49, 991.21) * mm});
            skLineSegment(sketch, "E658", {"start": v(-625.49, 991.21) * mm, "end": v(-624.85, 991.73) * mm});
            skLineSegment(sketch, "E659", {"start": v(-624.85, 991.73) * mm, "end": v(-624.22, 992.24) * mm});
            skLineSegment(sketch, "E660", {"start": v(-624.22, 992.24) * mm, "end": v(-623.57, 992.71) * mm});
            skLineSegment(sketch, "E661", {"start": v(-623.57, 992.71) * mm, "end": v(-622.88, 993.2) * mm});
            skLineSegment(sketch, "E662", {"start": v(-622.88, 993.2) * mm, "end": v(-622.2, 993.67) * mm});
            skLineSegment(sketch, "E663", {"start": v(-622.2, 993.67) * mm, "end": v(-621.5, 994.12) * mm});
            skLineSegment(sketch, "E664", {"start": v(-621.5, 994.12) * mm, "end": v(-620.78, 994.58) * mm});
            skLineSegment(sketch, "E665", {"start": v(-620.78, 994.58) * mm, "end": v(-620.04, 995.02) * mm});
            skLineSegment(sketch, "E666", {"start": v(-620.04, 995.02) * mm, "end": v(-619.3, 995.45) * mm});
            skLineSegment(sketch, "E667", {"start": v(-619.3, 995.45) * mm, "end": v(-618.54, 995.87) * mm});
            skLineSegment(sketch, "E668", {"start": v(-618.54, 995.87) * mm, "end": v(-617.76, 996.28) * mm});
            skLineSegment(sketch, "E669", {"start": v(-617.76, 996.28) * mm, "end": v(-616.99, 996.68) * mm});
            skLineSegment(sketch, "E670", {"start": v(-616.99, 996.68) * mm, "end": v(-616.2, 997.07) * mm});
            skLineSegment(sketch, "E671", {"start": v(-616.2, 997.07) * mm, "end": v(-615.38, 997.44) * mm});
            skLineSegment(sketch, "E672", {"start": v(-615.38, 997.44) * mm, "end": v(-614.55, 997.81) * mm});
            skLineSegment(sketch, "E673", {"start": v(-614.55, 997.81) * mm, "end": v(-613.72, 998.16) * mm});
            skLineSegment(sketch, "E674", {"start": v(-613.72, 998.16) * mm, "end": v(-612.86, 998.52) * mm});
            skLineSegment(sketch, "E675", {"start": v(-612.86, 998.52) * mm, "end": v(-612.01, 998.85) * mm});
            skLineSegment(sketch, "E676", {"start": v(-612.01, 998.85) * mm, "end": v(-611.13, 999.17) * mm});
            skLineSegment(sketch, "E677", {"start": v(-611.13, 999.17) * mm, "end": v(-610.25, 999.49) * mm});
            skLineSegment(sketch, "E678", {"start": v(-610.25, 999.49) * mm, "end": v(-609.35, 999.79) * mm});
            skLineSegment(sketch, "E679", {"start": v(-609.35, 999.79) * mm, "end": v(-608.45, 1000.07) * mm});
            skLineSegment(sketch, "E680", {"start": v(-608.45, 1000.07) * mm, "end": v(-604.48, 997.16) * mm});
            skLineSegment(sketch, "E681", {"start": v(-604.48, 997.16) * mm, "end": v(-600.64, 994.07) * mm});
            skLineSegment(sketch, "E682", {"start": v(-600.64, 994.07) * mm, "end": v(-600.69, 993.14) * mm});
            skLineSegment(sketch, "E683", {"start": v(-600.69, 993.14) * mm, "end": v(-600.74, 992.18) * mm});
            skLineSegment(sketch, "E684", {"start": v(-600.74, 992.18) * mm, "end": v(-600.81, 991.25) * mm});
            skLineSegment(sketch, "E685", {"start": v(-600.81, 991.25) * mm, "end": v(-600.9, 990.33) * mm});
            skLineSegment(sketch, "E686", {"start": v(-600.9, 990.33) * mm, "end": v(-601, 989.41) * mm});
            skLineSegment(sketch, "E687", {"start": v(-601, 989.41) * mm, "end": v(-601.11, 988.5) * mm});
            skLineSegment(sketch, "E688", {"start": v(-601.11, 988.5) * mm, "end": v(-601.24, 987.6) * mm});
            skLineSegment(sketch, "E689", {"start": v(-601.24, 987.6) * mm, "end": v(-601.38, 986.7) * mm});
            skLineSegment(sketch, "E690", {"start": v(-601.38, 986.7) * mm, "end": v(-601.53, 985.83) * mm});
            skLineSegment(sketch, "E691", {"start": v(-601.53, 985.83) * mm, "end": v(-601.71, 984.95) * mm});
            skLineSegment(sketch, "E692", {"start": v(-601.71, 984.95) * mm, "end": v(-601.89, 984.09) * mm});
            skLineSegment(sketch, "E693", {"start": v(-601.89, 984.09) * mm, "end": v(-602.08, 983.24) * mm});
            skLineSegment(sketch, "E694", {"start": v(-602.08, 983.24) * mm, "end": v(-602.3, 982.4) * mm});
            skLineSegment(sketch, "E695", {"start": v(-602.3, 982.4) * mm, "end": v(-602.5, 981.57) * mm});
            skLineSegment(sketch, "E696", {"start": v(-602.5, 981.57) * mm, "end": v(-602.75, 980.75) * mm});
            skLineSegment(sketch, "E697", {"start": v(-602.75, 980.75) * mm, "end": v(-603, 979.94) * mm});
            skLineSegment(sketch, "E698", {"start": v(-603, 979.94) * mm, "end": v(-603.26, 979.15) * mm});
            skLineSegment(sketch, "E699", {"start": v(-603.26, 979.15) * mm, "end": v(-603.53, 978.36) * mm});
            skLineSegment(sketch, "E700", {"start": v(-603.53, 978.36) * mm, "end": v(-603.83, 977.58) * mm});
            skLineSegment(sketch, "E701", {"start": v(-603.83, 977.58) * mm, "end": v(-604.13, 976.82) * mm});
            skLineSegment(sketch, "E702", {"start": v(-604.13, 976.82) * mm, "end": v(-604.45, 976.06) * mm});
            skLineSegment(sketch, "E703", {"start": v(-604.45, 976.06) * mm, "end": v(-604.78, 975.34) * mm});
            skLineSegment(sketch, "E704", {"start": v(-604.78, 975.34) * mm, "end": v(-605.13, 974.62) * mm});
            skLineSegment(sketch, "E705", {"start": v(-605.13, 974.62) * mm, "end": v(-605.49, 973.9) * mm});
            skLineSegment(sketch, "E706", {"start": v(-605.49, 973.9) * mm, "end": v(-605.87, 973.2) * mm});
            skLineSegment(sketch, "E707", {"start": v(-605.87, 973.2) * mm, "end": v(-606.26, 972.52) * mm});
            skLineSegment(sketch, "E708", {"start": v(-606.26, 972.52) * mm, "end": v(-606.67, 971.86) * mm});
            skLineSegment(sketch, "E709", {"start": v(-606.67, 971.86) * mm, "end": v(-607.1, 971.21) * mm});
            skLineSegment(sketch, "E710", {"start": v(-607.1, 971.21) * mm, "end": v(-607.53, 970.58) * mm});
            skLineSegment(sketch, "E711", {"start": v(-607.53, 970.58) * mm, "end": v(-607.94, 969.9) * mm});
            skLineSegment(sketch, "E712", {"start": v(-607.94, 969.9) * mm, "end": v(-618.57, 959.62) * mm});
            skLineSegment(sketch, "E713", {"start": v(-618.57, 959.62) * mm, "end": v(-607.62, 945.34) * mm});
            skLineSegment(sketch, "E714", {"start": v(-607.62, 945.34) * mm, "end": v(-594.92, 952.96) * mm});
            skLineSegment(sketch, "E715", {"start": v(-594.92, 952.96) * mm, "end": v(-594.18, 953.17) * mm});
            skLineSegment(sketch, "E716", {"start": v(-594.18, 953.17) * mm, "end": v(-593.46, 953.43) * mm});
            skLineSegment(sketch, "E717", {"start": v(-593.46, 953.43) * mm, "end": v(-592.72, 953.68) * mm});
            skLineSegment(sketch, "E718", {"start": v(-592.72, 953.68) * mm, "end": v(-591.97, 953.89) * mm});
            skLineSegment(sketch, "E719", {"start": v(-591.97, 953.89) * mm, "end": v(-591.22, 954.1) * mm});
            skLineSegment(sketch, "E720", {"start": v(-591.22, 954.1) * mm, "end": v(-590.44, 954.3) * mm});
            skLineSegment(sketch, "E721", {"start": v(-590.44, 954.3) * mm, "end": v(-589.66, 954.45) * mm});
            skLineSegment(sketch, "E722", {"start": v(-589.66, 954.45) * mm, "end": v(-588.87, 954.6) * mm});
            skLineSegment(sketch, "E723", {"start": v(-588.87, 954.6) * mm, "end": v(-588.08, 954.74) * mm});
            skLineSegment(sketch, "E724", {"start": v(-588.08, 954.74) * mm, "end": v(-587.27, 954.84) * mm});
            skLineSegment(sketch, "E725", {"start": v(-587.27, 954.84) * mm, "end": v(-586.45, 954.95) * mm});
            skLineSegment(sketch, "E726", {"start": v(-586.45, 954.95) * mm, "end": v(-585.62, 955.02) * mm});
            skLineSegment(sketch, "E727", {"start": v(-585.62, 955.02) * mm, "end": v(-584.8, 955.09) * mm});
            skLineSegment(sketch, "E728", {"start": v(-584.8, 955.09) * mm, "end": v(-583.97, 955.12) * mm});
            skLineSegment(sketch, "E729", {"start": v(-583.97, 955.12) * mm, "end": v(-583.12, 955.16) * mm});
            skLineSegment(sketch, "E730", {"start": v(-583.12, 955.16) * mm, "end": v(-582.26, 955.18) * mm});
            skLineSegment(sketch, "E731", {"start": v(-582.26, 955.18) * mm, "end": v(-581.4, 955.18) * mm});
            skLineSegment(sketch, "E732", {"start": v(-581.4, 955.18) * mm, "end": v(-580.53, 955.16) * mm});
            skLineSegment(sketch, "E733", {"start": v(-580.53, 955.16) * mm, "end": v(-579.66, 955.12) * mm});
            skLineSegment(sketch, "E734", {"start": v(-579.66, 955.12) * mm, "end": v(-578.78, 955.09) * mm});
            skLineSegment(sketch, "E735", {"start": v(-578.78, 955.09) * mm, "end": v(-577.9, 955.02) * mm});
            skLineSegment(sketch, "E736", {"start": v(-577.9, 955.02) * mm, "end": v(-577, 954.95) * mm});
            skLineSegment(sketch, "E737", {"start": v(-577, 954.95) * mm, "end": v(-576.12, 954.84) * mm});
            skLineSegment(sketch, "E738", {"start": v(-576.12, 954.84) * mm, "end": v(-575.2, 954.74) * mm});
            skLineSegment(sketch, "E739", {"start": v(-575.2, 954.74) * mm, "end": v(-574.3, 954.61) * mm});
            skLineSegment(sketch, "E740", {"start": v(-574.3, 954.61) * mm, "end": v(-573.38, 954.47) * mm});
            skLineSegment(sketch, "E741", {"start": v(-573.38, 954.47) * mm, "end": v(-572.47, 954.31) * mm});
            skLineSegment(sketch, "E742", {"start": v(-572.47, 954.31) * mm, "end": v(-571.55, 954.14) * mm});
            skLineSegment(sketch, "E743", {"start": v(-571.55, 954.14) * mm, "end": v(-570.63, 953.96) * mm});
            skLineSegment(sketch, "E744", {"start": v(-570.63, 953.96) * mm, "end": v(-569.7, 953.75) * mm});
            skLineSegment(sketch, "E745", {"start": v(-569.7, 953.75) * mm, "end": v(-567.72, 949.25) * mm});
            skLineSegment(sketch, "E746", {"start": v(-567.72, 949.25) * mm, "end": v(-565.92, 944.66) * mm});
            skLineSegment(sketch, "E747", {"start": v(-565.92, 944.66) * mm, "end": v(-566.43, 943.85) * mm});
            skLineSegment(sketch, "E748", {"start": v(-566.43, 943.85) * mm, "end": v(-566.96, 943.08) * mm});
            skLineSegment(sketch, "E749", {"start": v(-566.96, 943.08) * mm, "end": v(-567.5, 942.3) * mm});
            skLineSegment(sketch, "E750", {"start": v(-567.5, 942.3) * mm, "end": v(-568.04, 941.54) * mm});
            skLineSegment(sketch, "E751", {"start": v(-568.04, 941.54) * mm, "end": v(-568.57, 940.78) * mm});
            skLineSegment(sketch, "E752", {"start": v(-568.57, 940.78) * mm, "end": v(-569.13, 940.06) * mm});
            skLineSegment(sketch, "E753", {"start": v(-569.13, 940.06) * mm, "end": v(-569.7, 939.34) * mm});
            skLineSegment(sketch, "E754", {"start": v(-569.7, 939.34) * mm, "end": v(-570.26, 938.65) * mm});
            skLineSegment(sketch, "E755", {"start": v(-570.26, 938.65) * mm, "end": v(-570.83, 937.96) * mm});
            skLineSegment(sketch, "E756", {"start": v(-570.83, 937.96) * mm, "end": v(-571.4, 937.3) * mm});
            skLineSegment(sketch, "E757", {"start": v(-571.4, 937.3) * mm, "end": v(-572, 936.64) * mm});
            skLineSegment(sketch, "E758", {"start": v(-572, 936.64) * mm, "end": v(-572.59, 935.99) * mm});
            skLineSegment(sketch, "E759", {"start": v(-572.59, 935.99) * mm, "end": v(-573.19, 935.37) * mm});
            skLineSegment(sketch, "E760", {"start": v(-573.19, 935.37) * mm, "end": v(-573.8, 934.75) * mm});
            skLineSegment(sketch, "E761", {"start": v(-573.8, 934.75) * mm, "end": v(-574.42, 934.17) * mm});
            skLineSegment(sketch, "E762", {"start": v(-574.42, 934.17) * mm, "end": v(-575.04, 933.59) * mm});
            skLineSegment(sketch, "E763", {"start": v(-575.04, 933.59) * mm, "end": v(-575.66, 933.02) * mm});
            skLineSegment(sketch, "E764", {"start": v(-575.66, 933.02) * mm, "end": v(-576.3, 932.5) * mm});
            skLineSegment(sketch, "E765", {"start": v(-576.3, 932.5) * mm, "end": v(-576.93, 931.97) * mm});
            skLineSegment(sketch, "E766", {"start": v(-576.93, 931.97) * mm, "end": v(-577.58, 931.45) * mm});
            skLineSegment(sketch, "E767", {"start": v(-577.58, 931.45) * mm, "end": v(-578.23, 930.96) * mm});
            skLineSegment(sketch, "E768", {"start": v(-578.23, 930.96) * mm, "end": v(-578.89, 930.48) * mm});
            skLineSegment(sketch, "E769", {"start": v(-578.89, 930.48) * mm, "end": v(-579.56, 930.04) * mm});
            skLineSegment(sketch, "E770", {"start": v(-579.56, 930.04) * mm, "end": v(-580.23, 929.6) * mm});
            skLineSegment(sketch, "E771", {"start": v(-580.23, 929.6) * mm, "end": v(-580.9, 929.2) * mm});
            skLineSegment(sketch, "E772", {"start": v(-580.9, 929.2) * mm, "end": v(-581.57, 928.8) * mm});
            skLineSegment(sketch, "E773", {"start": v(-581.57, 928.8) * mm, "end": v(-582.26, 928.44) * mm});
            skLineSegment(sketch, "E774", {"start": v(-582.26, 928.44) * mm, "end": v(-582.96, 928.08) * mm});
            skLineSegment(sketch, "E775", {"start": v(-582.96, 928.08) * mm, "end": v(-583.65, 927.77) * mm});
            skLineSegment(sketch, "E776", {"start": v(-583.65, 927.77) * mm, "end": v(-584.34, 927.38) * mm});
            skLineSegment(sketch, "E777", {"start": v(-584.34, 927.38) * mm, "end": v(-598.7, 923.78) * mm});
            skLineSegment(sketch, "E778", {"start": v(-598.7, 923.78) * mm, "end": v(-596.35, 905.93) * mm});
            skLineSegment(sketch, "E779", {"start": v(-596.35, 905.93) * mm, "end": v(-581.55, 906.2) * mm});
            skLineSegment(sketch, "E780", {"start": v(-667.17, 904.59) * mm, "end": v(-667.2, 903.74) * mm});
            skLineSegment(sketch, "E781", {"start": v(-667.2, 903.74) * mm, "end": v(-667.54, 902.12) * mm});
            skLineSegment(sketch, "E782", {"start": v(-667.54, 902.12) * mm, "end": v(-668.16, 900.62) * mm});
            skLineSegment(sketch, "E783", {"start": v(-668.16, 900.62) * mm, "end": v(-669.06, 899.28) * mm});
            skLineSegment(sketch, "E784", {"start": v(-669.06, 899.28) * mm, "end": v(-670.2, 898.15) * mm});
            skLineSegment(sketch, "E785", {"start": v(-670.2, 898.15) * mm, "end": v(-671.53, 897.25) * mm});
            skLineSegment(sketch, "E786", {"start": v(-671.53, 897.25) * mm, "end": v(-673.03, 896.62) * mm});
            skLineSegment(sketch, "E787", {"start": v(-673.03, 896.62) * mm, "end": v(-674.65, 896.3) * mm});
            skLineSegment(sketch, "E788", {"start": v(-674.65, 896.3) * mm, "end": v(-675.51, 896.26) * mm});
            skLineSegment(sketch, "E789", {"start": v(-675.51, 896.26) * mm, "end": v(-676.36, 896.3) * mm});
            skLineSegment(sketch, "E790", {"start": v(-676.36, 896.3) * mm, "end": v(-677.98, 896.62) * mm});
            skLineSegment(sketch, "E791", {"start": v(-677.98, 896.62) * mm, "end": v(-679.48, 897.25) * mm});
            skLineSegment(sketch, "E792", {"start": v(-679.48, 897.25) * mm, "end": v(-680.82, 898.15) * mm});
            skLineSegment(sketch, "E793", {"start": v(-680.82, 898.15) * mm, "end": v(-681.95, 899.28) * mm});
            skLineSegment(sketch, "E794", {"start": v(-681.95, 899.28) * mm, "end": v(-682.85, 900.62) * mm});
            skLineSegment(sketch, "E795", {"start": v(-682.85, 900.62) * mm, "end": v(-683.47, 902.12) * mm});
            skLineSegment(sketch, "E796", {"start": v(-683.47, 902.12) * mm, "end": v(-683.8, 903.74) * mm});
            skLineSegment(sketch, "E797", {"start": v(-683.8, 903.74) * mm, "end": v(-683.84, 904.59) * mm});
            skLineSegment(sketch, "E798", {"start": v(-683.84, 904.59) * mm, "end": v(-683.8, 905.45) * mm});
            skLineSegment(sketch, "E799", {"start": v(-683.8, 905.45) * mm, "end": v(-683.47, 907.08) * mm});
            skLineSegment(sketch, "E800", {"start": v(-683.47, 907.08) * mm, "end": v(-682.85, 908.58) * mm});
            skLineSegment(sketch, "E801", {"start": v(-682.85, 908.58) * mm, "end": v(-681.95, 909.9) * mm});
            skLineSegment(sketch, "E802", {"start": v(-681.95, 909.9) * mm, "end": v(-680.82, 911.03) * mm});
            skLineSegment(sketch, "E803", {"start": v(-680.82, 911.03) * mm, "end": v(-679.48, 911.93) * mm});
            skLineSegment(sketch, "E804", {"start": v(-679.48, 911.93) * mm, "end": v(-677.98, 912.56) * mm});
            skLineSegment(sketch, "E805", {"start": v(-677.98, 912.56) * mm, "end": v(-676.36, 912.9) * mm});
            skLineSegment(sketch, "E806", {"start": v(-676.36, 912.9) * mm, "end": v(-675.51, 912.93) * mm});
            skLineSegment(sketch, "E807", {"start": v(-675.51, 912.93) * mm, "end": v(-674.65, 912.9) * mm});
            skLineSegment(sketch, "E808", {"start": v(-674.65, 912.9) * mm, "end": v(-673.03, 912.56) * mm});
            skLineSegment(sketch, "E809", {"start": v(-673.03, 912.56) * mm, "end": v(-671.53, 911.93) * mm});
            skLineSegment(sketch, "E810", {"start": v(-671.53, 911.93) * mm, "end": v(-670.2, 911.03) * mm});
            skLineSegment(sketch, "E811", {"start": v(-670.2, 911.03) * mm, "end": v(-669.06, 909.9) * mm});
            skLineSegment(sketch, "E812", {"start": v(-669.06, 909.9) * mm, "end": v(-668.16, 908.58) * mm});
            skLineSegment(sketch, "E813", {"start": v(-668.16, 908.58) * mm, "end": v(-667.54, 907.08) * mm});
            skLineSegment(sketch, "E814", {"start": v(-667.54, 907.08) * mm, "end": v(-667.2, 905.45) * mm});
            skLineSegment(sketch, "E815", {"start": v(-667.2, 905.45) * mm, "end": v(-667.17, 904.59) * mm});
            skSolve(sketch);
        }
        {
            var Q0;
            Q0 = qSketchRegion(id + "F0", true);
            extrude(context, id + "F1", {"entities" : qUnion([Q0]), "depth" : 25 * mm, "offsetDistance" : 25 * mm});
        }
    });
